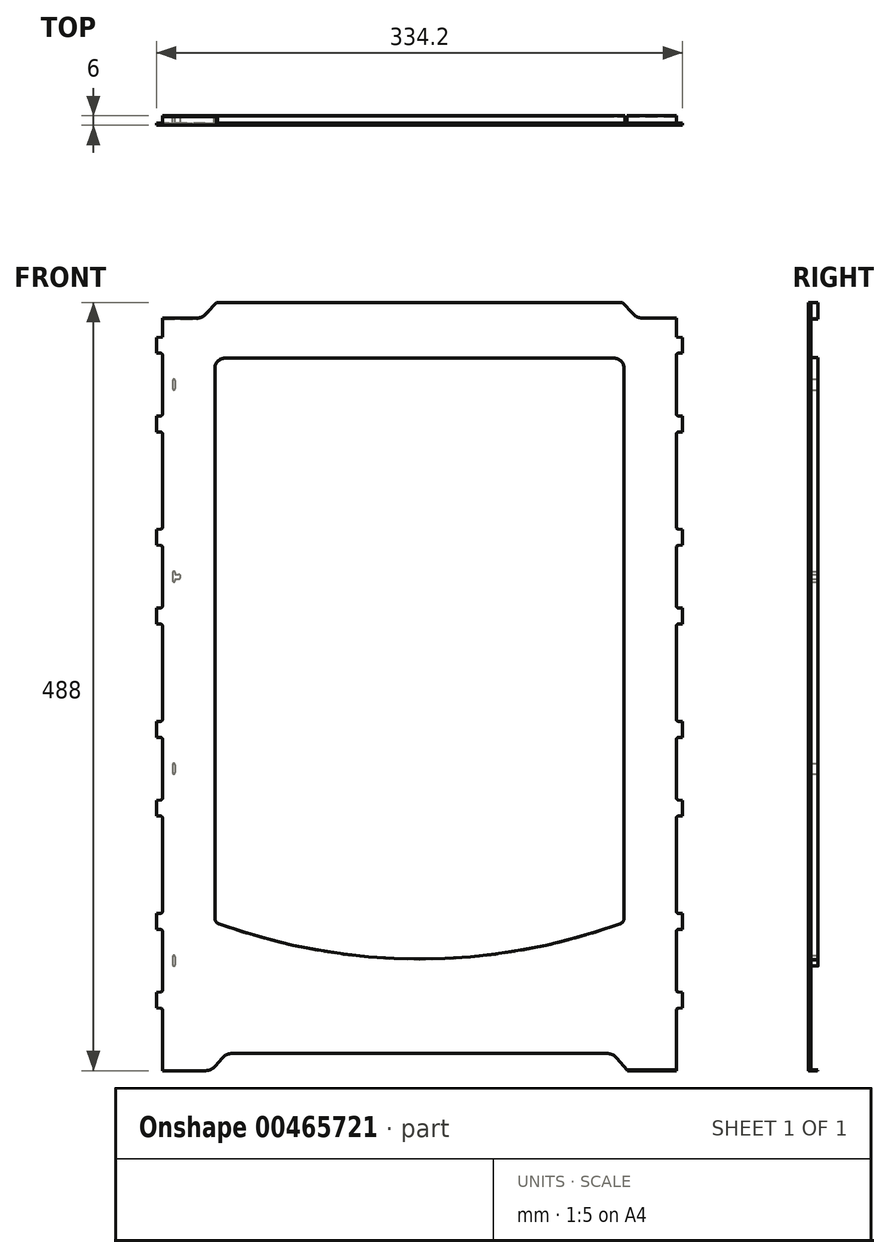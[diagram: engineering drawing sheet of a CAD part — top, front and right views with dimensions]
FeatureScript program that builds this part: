
annotation { "Feature Type Name" : "Feature", "Feature Type Description" : "" }
export const myFeature = defineFeature(function(context is Context, id is Id, definition is map)
    precondition{}
    {
        {
            var Q0;
            Q0=qCreatedBy(makeId("Front.planeOp"),FACE);
            var sketch = newSketch(context, id + "F0", { "sketchPlane" : qUnion([Q0])});
            skLineSegment(sketch, "E0.bottom", {"start": v(163.1, 244) * mm, "end": v(-163.1, 244) * mm});
            skLineSegment(sketch, "E0.top", {"start": v(163.1, -244) * mm, "end": v(-163.1, -244) * mm});
            skLineSegment(sketch, "E0.left", {"start": v(163.1, 244) * mm, "end": v(163.1, -244) * mm});
            skLineSegment(sketch, "E0.right", {"start": v(-163.1, 244) * mm, "end": v(-163.1, -244) * mm});
            skPoint(sketch, "E0.middle", {"position": v(0, 0) * mm});
            skSolve(sketch);
        }
        {
            var Q0;
            Q0=makeQuery(id+"F0.imprint","IMPRINT",FACE,{"disambiguationData":[TD([[makeQuery(id+"F0.imprint","IMPRINT",EDGE,{"derivedFrom":sQuery(id+"F0.wireOp",EDGE,"E0.bottom")}),1.0]])]});
            extrude(context, id + "F1", {"entities" : qUnion([Q0]), "depth" : 6 * mm});
        }
        {
            var Q0;
            Q0=makeQuery(id+"F1.opExtrude","CAP_FACE",FACE,{"disambiguationData":[OSD([sQuery(id+"F0.wireOp",EDGE,"E0.bottom"),sQuery(id+"F0.wireOp",EDGE,"E0.top"),sQuery(id+"F0.wireOp",EDGE,"E0.left"),sQuery(id+"F0.wireOp",EDGE,"E0.right")])],"isStart":false});
            var sketch = newSketch(context, id + "F2", { "sketchPlane" : qUnion([Q0])});
            skLineSegment(sketch, "E1", {"start": v(-167.1, -204.2) * mm, "end": v(-163.1, -204.34) * mm});
            skLineSegment(sketch, "E2", {"start": v(-167.1, -204.2) * mm, "end": v(-167.1, -194.2) * mm});
            skLineSegment(sketch, "E3", {"start": v(-167.1, -199.2) * mm, "end": v(-163.1, -199.2) * mm, "construction": true});
            skLineSegment(sketch, "E4.MirrorCS", {"start": v(-167.1, -194.2) * mm, "end": v(-163.1, -194.06) * mm});
            skLineSegment(sketch, "E5", {"start": v(0, 244) * mm, "end": v(0, -244) * mm, "construction": true});
            skLineSegment(sketch, "E6.MirrorCS", {"start": v(167.1, -204.2) * mm, "end": v(167.1, -194.2) * mm});
            skLineSegment(sketch, "E7.MirrorCS", {"start": v(167.1, -199.2) * mm, "end": v(163.1, -199.2) * mm, "construction": true});
            skLineSegment(sketch, "E8.MirrorCS", {"start": v(167.1, -204.2) * mm, "end": v(163.1, -204.34) * mm});
            skLineSegment(sketch, "E9.MirrorCS", {"start": v(167.1, -194.2) * mm, "end": v(163.1, -194.06) * mm});
            skLineSegment(sketch, "E10", {"start": v(-163.1, -154.34) * mm, "end": v(-167.1, -154.2) * mm});
            skLineSegment(sketch, "E11", {"start": v(-167.1, -154.2) * mm, "end": v(-167.1, -144.2) * mm});
            skLineSegment(sketch, "E12", {"start": v(-167.1, -144.2) * mm, "end": v(-163.1, -144.06) * mm});
            skLineSegment(sketch, "E13", {"start": v(-163.1, -82.34) * mm, "end": v(-167.1, -82.2) * mm});
            skLineSegment(sketch, "E14", {"start": v(-167.1, -82.2) * mm, "end": v(-167.1, -72.2) * mm});
            skLineSegment(sketch, "E15", {"start": v(-167.1, -72.2) * mm, "end": v(-163.1, -72.06) * mm});
            skLineSegment(sketch, "E16", {"start": v(-163.1, -32.34) * mm, "end": v(-167.1, -32.2) * mm});
            skLineSegment(sketch, "E17", {"start": v(-167.1, -32.2) * mm, "end": v(-167.1, -22.2) * mm});
            skLineSegment(sketch, "E18", {"start": v(-167.1, -22.2) * mm, "end": v(-163.1, -22.06) * mm});
            skLineSegment(sketch, "E19", {"start": v(-163.1, 39.66) * mm, "end": v(-167.1, 39.8) * mm});
            skLineSegment(sketch, "E20", {"start": v(-167.1, 39.8) * mm, "end": v(-167.1, 49.8) * mm});
            skLineSegment(sketch, "E21", {"start": v(-167.1, 49.8) * mm, "end": v(-163.1, 49.94) * mm});
            skLineSegment(sketch, "E22", {"start": v(-163.1, 89.66) * mm, "end": v(-167.1, 89.8) * mm});
            skLineSegment(sketch, "E23", {"start": v(-167.1, 89.8) * mm, "end": v(-167.1, 99.8) * mm});
            skLineSegment(sketch, "E24", {"start": v(-167.1, 99.8) * mm, "end": v(-163.1, 99.94) * mm});
            skLineSegment(sketch, "E25", {"start": v(-163.1, 161.66) * mm, "end": v(-167.1, 161.8) * mm});
            skLineSegment(sketch, "E26", {"start": v(-167.1, 161.8) * mm, "end": v(-167.1, 171.8) * mm});
            skLineSegment(sketch, "E27", {"start": v(-167.1, 171.8) * mm, "end": v(-163.1, 171.94) * mm});
            skLineSegment(sketch, "E28", {"start": v(-163.1, 211.66) * mm, "end": v(-167.1, 211.8) * mm});
            skLineSegment(sketch, "E29", {"start": v(-167.1, 211.8) * mm, "end": v(-167.1, 221.8) * mm});
            skLineSegment(sketch, "E30", {"start": v(-167.1, 221.8) * mm, "end": v(-163.1, 221.94) * mm});
            skLineSegment(sketch, "E31.MirrorCS", {"start": v(163.1, 211.66) * mm, "end": v(167.1, 211.8) * mm});
            skLineSegment(sketch, "E32.MirrorCS", {"start": v(167.1, 99.8) * mm, "end": v(163.1, 99.94) * mm});
            skLineSegment(sketch, "E33.MirrorCS", {"start": v(167.1, 221.8) * mm, "end": v(163.1, 221.94) * mm});
            skLineSegment(sketch, "E34.MirrorCS", {"start": v(163.1, -32.34) * mm, "end": v(167.1, -32.2) * mm});
            skLineSegment(sketch, "E35.MirrorCS", {"start": v(163.1, -154.34) * mm, "end": v(167.1, -154.2) * mm});
            skLineSegment(sketch, "E36.MirrorCS", {"start": v(167.1, -154.2) * mm, "end": v(167.1, -144.2) * mm});
            skLineSegment(sketch, "E37.MirrorCS", {"start": v(167.1, -72.2) * mm, "end": v(163.1, -72.06) * mm});
            skLineSegment(sketch, "E38.MirrorCS", {"start": v(167.1, -144.2) * mm, "end": v(163.1, -144.06) * mm});
            skLineSegment(sketch, "E39.MirrorCS", {"start": v(167.1, -82.2) * mm, "end": v(167.1, -72.2) * mm});
            skLineSegment(sketch, "E40.MirrorCS", {"start": v(167.1, 39.8) * mm, "end": v(167.1, 49.8) * mm});
            skLineSegment(sketch, "E41.MirrorCS", {"start": v(167.1, 171.8) * mm, "end": v(163.1, 171.94) * mm});
            skLineSegment(sketch, "E42.MirrorCS", {"start": v(167.1, 161.8) * mm, "end": v(167.1, 171.8) * mm});
            skLineSegment(sketch, "E43.MirrorCS", {"start": v(163.1, -82.34) * mm, "end": v(167.1, -82.2) * mm});
            skLineSegment(sketch, "E44.MirrorCS", {"start": v(167.1, 49.8) * mm, "end": v(163.1, 49.94) * mm});
            skLineSegment(sketch, "E45.MirrorCS", {"start": v(167.1, -22.2) * mm, "end": v(163.1, -22.06) * mm});
            skLineSegment(sketch, "E46.MirrorCS", {"start": v(163.1, 89.66) * mm, "end": v(167.1, 89.8) * mm});
            skLineSegment(sketch, "E47.MirrorCS", {"start": v(163.1, 161.66) * mm, "end": v(167.1, 161.8) * mm});
            skLineSegment(sketch, "E48.MirrorCS", {"start": v(167.1, 211.8) * mm, "end": v(167.1, 221.8) * mm});
            skLineSegment(sketch, "E49.MirrorCS", {"start": v(167.1, 89.8) * mm, "end": v(167.1, 99.8) * mm});
            skLineSegment(sketch, "E50.MirrorCS", {"start": v(167.1, -32.2) * mm, "end": v(167.1, -22.2) * mm});
            skLineSegment(sketch, "E51.MirrorCS", {"start": v(163.1, 39.66) * mm, "end": v(167.1, 39.8) * mm});
            skSolve(sketch);
        }
        {
            var Q0;
            {var subQ0=sQuery(id+"F2.wireOp",EDGE,"E28");Q0=makeQuery(id+"F2.imprint","IMPRINT",FACE,{"disambiguationData":[TD([[makeQuery(id+"F2.imprint","IMPRINT",EDGE,{"derivedFrom":subQ0}),-1.0]])]});}
            var Q1;
            {var subQ0=sQuery(id+"F2.wireOp",EDGE,"E25");Q1=makeQuery(id+"F2.imprint","IMPRINT",FACE,{"disambiguationData":[TD([[makeQuery(id+"F2.imprint","IMPRINT",EDGE,{"derivedFrom":subQ0}),-1.0]])]});}
            var Q2;
            {var subQ0=sQuery(id+"F2.wireOp",EDGE,"E22");Q2=makeQuery(id+"F2.imprint","IMPRINT",FACE,{"disambiguationData":[TD([[makeQuery(id+"F2.imprint","IMPRINT",EDGE,{"derivedFrom":subQ0}),-1.0]])]});}
            var Q3;
            {var subQ0=sQuery(id+"F2.wireOp",EDGE,"E19");Q3=makeQuery(id+"F2.imprint","IMPRINT",FACE,{"disambiguationData":[TD([[makeQuery(id+"F2.imprint","IMPRINT",EDGE,{"derivedFrom":subQ0}),-1.0]])]});}
            var Q4;
            {var subQ0=sQuery(id+"F2.wireOp",EDGE,"E16");Q4=makeQuery(id+"F2.imprint","IMPRINT",FACE,{"disambiguationData":[TD([[makeQuery(id+"F2.imprint","IMPRINT",EDGE,{"derivedFrom":subQ0}),-1.0]])]});}
            var Q5;
            {var subQ0=sQuery(id+"F2.wireOp",EDGE,"E13");Q5=makeQuery(id+"F2.imprint","IMPRINT",FACE,{"disambiguationData":[TD([[makeQuery(id+"F2.imprint","IMPRINT",EDGE,{"derivedFrom":subQ0}),-1.0]])]});}
            var Q6;
            {var subQ0=sQuery(id+"F2.wireOp",EDGE,"E10");Q6=makeQuery(id+"F2.imprint","IMPRINT",FACE,{"disambiguationData":[TD([[makeQuery(id+"F2.imprint","IMPRINT",EDGE,{"derivedFrom":subQ0}),-1.0]])]});}
            var Q7;
            {var subQ0=sQuery(id+"F2.wireOp",EDGE,"E1");Q7=makeQuery(id+"F2.imprint","IMPRINT",FACE,{"disambiguationData":[TD([[makeQuery(id+"F2.imprint","IMPRINT",EDGE,{"derivedFrom":subQ0}),1.0]])]});}
            var Q8;
            Q8=makeQuery(id+"F2.imprint","IMPRINT",FACE,{"disambiguationData":[TD([[makeQuery(id+"F2.imprint","IMPRINT",EDGE,{"derivedFrom":sQuery(id+"F2.wireOp",EDGE,"E6.MirrorCS")}),1.0]])]});
            var Q9;
            {var subQ0=sQuery(id+"F2.wireOp",EDGE,"E35.MirrorCS");Q9=makeQuery(id+"F2.imprint","IMPRINT",FACE,{"disambiguationData":[TD([[makeQuery(id+"F2.imprint","IMPRINT",EDGE,{"derivedFrom":subQ0}),1.0]])]});}
            var Q10;
            {var subQ0=sQuery(id+"F2.wireOp",EDGE,"E37.MirrorCS");Q10=makeQuery(id+"F2.imprint","IMPRINT",FACE,{"disambiguationData":[TD([[makeQuery(id+"F2.imprint","IMPRINT",EDGE,{"derivedFrom":subQ0}),1.0]])]});}
            var Q11;
            {var subQ0=sQuery(id+"F2.wireOp",EDGE,"E34.MirrorCS");Q11=makeQuery(id+"F2.imprint","IMPRINT",FACE,{"disambiguationData":[TD([[makeQuery(id+"F2.imprint","IMPRINT",EDGE,{"derivedFrom":subQ0}),1.0]])]});}
            var Q12;
            Q12=makeQuery(id+"F2.imprint","IMPRINT",FACE,{"disambiguationData":[TD([[makeQuery(id+"F2.imprint","IMPRINT",EDGE,{"derivedFrom":sQuery(id+"F2.wireOp",EDGE,"E40.MirrorCS")}),1.0]])]});
            var Q13;
            {var subQ0=sQuery(id+"F2.wireOp",EDGE,"E32.MirrorCS");Q13=makeQuery(id+"F2.imprint","IMPRINT",FACE,{"disambiguationData":[TD([[makeQuery(id+"F2.imprint","IMPRINT",EDGE,{"derivedFrom":subQ0}),1.0]])]});}
            var Q14;
            {var subQ0=sQuery(id+"F2.wireOp",EDGE,"E41.MirrorCS");Q14=makeQuery(id+"F2.imprint","IMPRINT",FACE,{"disambiguationData":[TD([[makeQuery(id+"F2.imprint","IMPRINT",EDGE,{"derivedFrom":subQ0}),1.0]])]});}
            var Q15;
            {var subQ0=sQuery(id+"F2.wireOp",EDGE,"E31.MirrorCS");Q15=makeQuery(id+"F2.imprint","IMPRINT",FACE,{"disambiguationData":[TD([[makeQuery(id+"F2.imprint","IMPRINT",EDGE,{"derivedFrom":subQ0}),1.0]])]});}
            extrude(context, id + "F3", {"entities" : qUnion([Q0, Q1, Q2, Q3, Q4, Q5, Q6, Q7, Q8, Q9, Q10, Q11, Q12, Q13, Q14, Q15]), "operationType" : NewBodyOperationType.ADD, "oppositeDirection" : true, "depth" : 6 * mm});
        }
        {
            var Q0;
            Q0=makeQuery(id+"F3.opExtrude","SWEPT_EDGE",EDGE,{"disambiguationData":[OSD([sQuery(id+"F0.wireOp",EDGE,"E0.right"),sQuery(id+"F2.wireOp",EDGE,"E1")])]});
            var Q1;
            Q1=makeQuery(id+"F3.opExtrude","SWEPT_EDGE",EDGE,{"disambiguationData":[OSD([sQuery(id+"F0.wireOp",EDGE,"E0.right"),sQuery(id+"F2.wireOp",EDGE,"E4.MirrorCS")])]});
            var Q2;
            Q2=makeQuery(id+"F3.opExtrude","SWEPT_EDGE",EDGE,{"disambiguationData":[OSD([sQuery(id+"F0.wireOp",EDGE,"E0.right"),sQuery(id+"F2.wireOp",EDGE,"E10")])]});
            var Q3;
            Q3=makeQuery(id+"F3.opExtrude","SWEPT_EDGE",EDGE,{"disambiguationData":[OSD([sQuery(id+"F0.wireOp",EDGE,"E0.right"),sQuery(id+"F2.wireOp",EDGE,"E15")])]});
            var Q4;
            Q4=makeQuery(id+"F3.opExtrude","SWEPT_EDGE",EDGE,{"disambiguationData":[OSD([sQuery(id+"F0.wireOp",EDGE,"E0.right"),sQuery(id+"F2.wireOp",EDGE,"E13")])]});
            var Q5;
            Q5=makeQuery(id+"F3.opExtrude","SWEPT_EDGE",EDGE,{"disambiguationData":[OSD([sQuery(id+"F0.wireOp",EDGE,"E0.right"),sQuery(id+"F2.wireOp",EDGE,"E12")])]});
            var Q6;
            Q6=makeQuery(id+"F3.opExtrude","SWEPT_EDGE",EDGE,{"disambiguationData":[OSD([sQuery(id+"F0.wireOp",EDGE,"E0.right"),sQuery(id+"F2.wireOp",EDGE,"E18")])]});
            var Q7;
            Q7=makeQuery(id+"F3.opExtrude","SWEPT_EDGE",EDGE,{"disambiguationData":[OSD([sQuery(id+"F0.wireOp",EDGE,"E0.right"),sQuery(id+"F2.wireOp",EDGE,"E16")])]});
            var Q8;
            Q8=makeQuery(id+"F3.opExtrude","SWEPT_EDGE",EDGE,{"disambiguationData":[OSD([sQuery(id+"F0.wireOp",EDGE,"E0.right"),sQuery(id+"F2.wireOp",EDGE,"E19")])]});
            var Q9;
            Q9=makeQuery(id+"F3.opExtrude","SWEPT_EDGE",EDGE,{"disambiguationData":[OSD([sQuery(id+"F0.wireOp",EDGE,"E0.right"),sQuery(id+"F2.wireOp",EDGE,"E22")])]});
            var Q10;
            Q10=makeQuery(id+"F3.opExtrude","SWEPT_EDGE",EDGE,{"disambiguationData":[OSD([sQuery(id+"F0.wireOp",EDGE,"E0.right"),sQuery(id+"F2.wireOp",EDGE,"E25")])]});
            var Q11;
            Q11=makeQuery(id+"F3.opExtrude","SWEPT_EDGE",EDGE,{"disambiguationData":[OSD([sQuery(id+"F0.wireOp",EDGE,"E0.right"),sQuery(id+"F2.wireOp",EDGE,"E30")])]});
            var Q12;
            Q12=makeQuery(id+"F3.opExtrude","SWEPT_EDGE",EDGE,{"disambiguationData":[OSD([sQuery(id+"F0.wireOp",EDGE,"E0.right"),sQuery(id+"F2.wireOp",EDGE,"E27")])]});
            var Q13;
            Q13=makeQuery(id+"F3.opExtrude","SWEPT_EDGE",EDGE,{"disambiguationData":[OSD([sQuery(id+"F0.wireOp",EDGE,"E0.right"),sQuery(id+"F2.wireOp",EDGE,"E24")])]});
            var Q14;
            Q14=makeQuery(id+"F3.opExtrude","SWEPT_EDGE",EDGE,{"disambiguationData":[OSD([sQuery(id+"F0.wireOp",EDGE,"E0.right"),sQuery(id+"F2.wireOp",EDGE,"E21")])]});
            var Q15;
            Q15=makeQuery(id+"F3.opExtrude","SWEPT_EDGE",EDGE,{"disambiguationData":[OSD([sQuery(id+"F0.wireOp",EDGE,"E0.right"),sQuery(id+"F2.wireOp",EDGE,"E28")])]});
            var Q16;
            Q16=makeQuery(id+"F3.opExtrude","SWEPT_EDGE",EDGE,{"disambiguationData":[OSD([sQuery(id+"F0.wireOp",EDGE,"E0.left"),sQuery(id+"F2.wireOp",EDGE,"E33.MirrorCS")])]});
            var Q17;
            Q17=makeQuery(id+"F3.opExtrude","SWEPT_EDGE",EDGE,{"disambiguationData":[OSD([sQuery(id+"F0.wireOp",EDGE,"E0.left"),sQuery(id+"F2.wireOp",EDGE,"E41.MirrorCS")])]});
            var Q18;
            Q18=makeQuery(id+"F3.opExtrude","SWEPT_EDGE",EDGE,{"disambiguationData":[OSD([sQuery(id+"F0.wireOp",EDGE,"E0.left"),sQuery(id+"F2.wireOp",EDGE,"E32.MirrorCS")])]});
            var Q19;
            Q19=makeQuery(id+"F3.opExtrude","SWEPT_EDGE",EDGE,{"disambiguationData":[OSD([sQuery(id+"F0.wireOp",EDGE,"E0.left"),sQuery(id+"F2.wireOp",EDGE,"E44.MirrorCS")])]});
            var Q20;
            Q20=makeQuery(id+"F3.opExtrude","SWEPT_EDGE",EDGE,{"disambiguationData":[OSD([sQuery(id+"F0.wireOp",EDGE,"E0.left"),sQuery(id+"F2.wireOp",EDGE,"E45.MirrorCS")])]});
            var Q21;
            Q21=makeQuery(id+"F3.opExtrude","SWEPT_EDGE",EDGE,{"disambiguationData":[OSD([sQuery(id+"F0.wireOp",EDGE,"E0.left"),sQuery(id+"F2.wireOp",EDGE,"E37.MirrorCS")])]});
            var Q22;
            Q22=makeQuery(id+"F3.opExtrude","SWEPT_EDGE",EDGE,{"disambiguationData":[OSD([sQuery(id+"F0.wireOp",EDGE,"E0.left"),sQuery(id+"F2.wireOp",EDGE,"E9.MirrorCS")])]});
            var Q23;
            Q23=makeQuery(id+"F3.opExtrude","SWEPT_EDGE",EDGE,{"disambiguationData":[OSD([sQuery(id+"F0.wireOp",EDGE,"E0.left"),sQuery(id+"F2.wireOp",EDGE,"E38.MirrorCS")])]});
            var Q24;
            Q24=makeQuery(id+"F3.opExtrude","SWEPT_EDGE",EDGE,{"disambiguationData":[OSD([sQuery(id+"F0.wireOp",EDGE,"E0.left"),sQuery(id+"F2.wireOp",EDGE,"E8.MirrorCS")])]});
            var Q25;
            Q25=makeQuery(id+"F3.opExtrude","SWEPT_EDGE",EDGE,{"disambiguationData":[OSD([sQuery(id+"F0.wireOp",EDGE,"E0.left"),sQuery(id+"F2.wireOp",EDGE,"E35.MirrorCS")])]});
            var Q26;
            Q26=makeQuery(id+"F3.opExtrude","SWEPT_EDGE",EDGE,{"disambiguationData":[OSD([sQuery(id+"F0.wireOp",EDGE,"E0.left"),sQuery(id+"F2.wireOp",EDGE,"E43.MirrorCS")])]});
            var Q27;
            Q27=makeQuery(id+"F3.opExtrude","SWEPT_EDGE",EDGE,{"disambiguationData":[OSD([sQuery(id+"F0.wireOp",EDGE,"E0.left"),sQuery(id+"F2.wireOp",EDGE,"E34.MirrorCS")])]});
            var Q28;
            Q28=makeQuery(id+"F3.opExtrude","SWEPT_EDGE",EDGE,{"disambiguationData":[OSD([sQuery(id+"F0.wireOp",EDGE,"E0.left"),sQuery(id+"F2.wireOp",EDGE,"E51.MirrorCS")])]});
            var Q29;
            Q29=makeQuery(id+"F3.opExtrude","SWEPT_EDGE",EDGE,{"disambiguationData":[OSD([sQuery(id+"F0.wireOp",EDGE,"E0.left"),sQuery(id+"F2.wireOp",EDGE,"E46.MirrorCS")])]});
            var Q30;
            Q30=makeQuery(id+"F3.opExtrude","SWEPT_EDGE",EDGE,{"disambiguationData":[OSD([sQuery(id+"F0.wireOp",EDGE,"E0.left"),sQuery(id+"F2.wireOp",EDGE,"E47.MirrorCS")])]});
            var Q31;
            Q31=makeQuery(id+"F3.opExtrude","SWEPT_EDGE",EDGE,{"disambiguationData":[OSD([sQuery(id+"F0.wireOp",EDGE,"E0.left"),sQuery(id+"F2.wireOp",EDGE,"E31.MirrorCS")])]});
            fillet(context, id + "F4", {"entities" : qUnion([Q0, Q1, Q2, Q3, Q4, Q5, Q6, Q7, Q8, Q9, Q10, Q11, Q12, Q13, Q14, Q15, Q16, Q17, Q18, Q19, Q20, Q21, Q22, Q23, Q24, Q25, Q26, Q27, Q28, Q29, Q30, Q31]), "radius" : 1.5 * mm, "tangentPropagation" : true, "allowEdgeOverflow" : false});
        }
        {
            var Q0;
            {var subQ0=sQuery(id+"F0.wireOp",EDGE,"E0.left");var subQ1=sQuery(id+"F0.wireOp",EDGE,"E0.right");Q0=makeQuery(id+"F3.boolean.opBoolean","MERGE",FACE,{"derivedFrom":[makeQuery(id+"F1.opExtrude","CAP_FACE",FACE,{"disambiguationData":[OSD([sQuery(id+"F0.wireOp",EDGE,"E0.bottom"),sQuery(id+"F0.wireOp",EDGE,"E0.top"),subQ0,subQ1])],"isStart":false}),makeQuery(id+"F3.opExtrude","CAP_FACE",FACE,{"disambiguationData":[OSD([subQ1,sQuery(id+"F2.wireOp",EDGE,"E1"),sQuery(id+"F2.wireOp",EDGE,"E2"),sQuery(id+"F2.wireOp",EDGE,"E4.MirrorCS")])],"isStart":true}),makeQuery(id+"F3.opExtrude","CAP_FACE",FACE,{"disambiguationData":[OSD([subQ0,sQuery(id+"F2.wireOp",EDGE,"E6.MirrorCS"),sQuery(id+"F2.wireOp",EDGE,"E8.MirrorCS"),sQuery(id+"F2.wireOp",EDGE,"E9.MirrorCS")])],"isStart":true}),makeQuery(id+"F3.opExtrude","CAP_FACE",FACE,{"disambiguationData":[OSD([subQ1,sQuery(id+"F2.wireOp",EDGE,"E10"),sQuery(id+"F2.wireOp",EDGE,"E11"),sQuery(id+"F2.wireOp",EDGE,"E12")])],"isStart":true}),makeQuery(id+"F3.opExtrude","CAP_FACE",FACE,{"disambiguationData":[OSD([subQ1,sQuery(id+"F2.wireOp",EDGE,"E13"),sQuery(id+"F2.wireOp",EDGE,"E14"),sQuery(id+"F2.wireOp",EDGE,"E15")])],"isStart":true}),makeQuery(id+"F3.opExtrude","CAP_FACE",FACE,{"disambiguationData":[OSD([subQ1,sQuery(id+"F2.wireOp",EDGE,"E16"),sQuery(id+"F2.wireOp",EDGE,"E17"),sQuery(id+"F2.wireOp",EDGE,"E18")])],"isStart":true}),makeQuery(id+"F3.opExtrude","CAP_FACE",FACE,{"disambiguationData":[OSD([subQ1,sQuery(id+"F2.wireOp",EDGE,"E19"),sQuery(id+"F2.wireOp",EDGE,"E20"),sQuery(id+"F2.wireOp",EDGE,"E21")])],"isStart":true}),makeQuery(id+"F3.opExtrude","CAP_FACE",FACE,{"disambiguationData":[OSD([subQ1,sQuery(id+"F2.wireOp",EDGE,"E22"),sQuery(id+"F2.wireOp",EDGE,"E23"),sQuery(id+"F2.wireOp",EDGE,"E24")])],"isStart":true}),makeQuery(id+"F3.opExtrude","CAP_FACE",FACE,{"disambiguationData":[OSD([subQ1,sQuery(id+"F2.wireOp",EDGE,"E25"),sQuery(id+"F2.wireOp",EDGE,"E26"),sQuery(id+"F2.wireOp",EDGE,"E27")])],"isStart":true}),makeQuery(id+"F3.opExtrude","CAP_FACE",FACE,{"disambiguationData":[OSD([subQ1,sQuery(id+"F2.wireOp",EDGE,"E28"),sQuery(id+"F2.wireOp",EDGE,"E29"),sQuery(id+"F2.wireOp",EDGE,"E30")])],"isStart":true}),makeQuery(id+"F3.opExtrude","CAP_FACE",FACE,{"disambiguationData":[OSD([subQ0,sQuery(id+"F2.wireOp",EDGE,"E31.MirrorCS"),sQuery(id+"F2.wireOp",EDGE,"E33.MirrorCS"),sQuery(id+"F2.wireOp",EDGE,"E48.MirrorCS")])],"isStart":true}),makeQuery(id+"F3.opExtrude","CAP_FACE",FACE,{"disambiguationData":[OSD([subQ0,sQuery(id+"F2.wireOp",EDGE,"E32.MirrorCS"),sQuery(id+"F2.wireOp",EDGE,"E46.MirrorCS"),sQuery(id+"F2.wireOp",EDGE,"E49.MirrorCS")])],"isStart":true}),makeQuery(id+"F3.opExtrude","CAP_FACE",FACE,{"disambiguationData":[OSD([subQ0,sQuery(id+"F2.wireOp",EDGE,"E34.MirrorCS"),sQuery(id+"F2.wireOp",EDGE,"E45.MirrorCS"),sQuery(id+"F2.wireOp",EDGE,"E50.MirrorCS")])],"isStart":true}),makeQuery(id+"F3.opExtrude","CAP_FACE",FACE,{"disambiguationData":[OSD([subQ0,sQuery(id+"F2.wireOp",EDGE,"E35.MirrorCS"),sQuery(id+"F2.wireOp",EDGE,"E36.MirrorCS"),sQuery(id+"F2.wireOp",EDGE,"E38.MirrorCS")])],"isStart":true}),makeQuery(id+"F3.opExtrude","CAP_FACE",FACE,{"disambiguationData":[OSD([subQ0,sQuery(id+"F2.wireOp",EDGE,"E37.MirrorCS"),sQuery(id+"F2.wireOp",EDGE,"E39.MirrorCS"),sQuery(id+"F2.wireOp",EDGE,"E43.MirrorCS")])],"isStart":true}),makeQuery(id+"F3.opExtrude","CAP_FACE",FACE,{"disambiguationData":[OSD([subQ0,sQuery(id+"F2.wireOp",EDGE,"E40.MirrorCS"),sQuery(id+"F2.wireOp",EDGE,"E44.MirrorCS"),sQuery(id+"F2.wireOp",EDGE,"E51.MirrorCS")])],"isStart":true}),makeQuery(id+"F3.opExtrude","CAP_FACE",FACE,{"disambiguationData":[OSD([subQ0,sQuery(id+"F2.wireOp",EDGE,"E41.MirrorCS"),sQuery(id+"F2.wireOp",EDGE,"E42.MirrorCS"),sQuery(id+"F2.wireOp",EDGE,"E47.MirrorCS")])],"isStart":true})]});}
            var sketch = newSketch(context, id + "F5", { "sketchPlane" : qUnion([Q0])});
            skLineSegment(sketch, "E52.bottom", {"start": v(130, -173) * mm, "end": v(-130, -173) * mm, "construction": true});
            skLineSegment(sketch, "E52.top", {"start": v(130, 208.5) * mm, "end": v(-130, 208.5) * mm});
            skLineSegment(sketch, "E52.left", {"start": v(130, -173) * mm, "end": v(130, 208.5) * mm});
            skLineSegment(sketch, "E52.right", {"start": v(-130, -173) * mm, "end": v(-130, 208.5) * mm});
            skPoint(sketch, "E52.middle", {"position": v(0, 17.75) * mm});
            skArc(sketch, "E53", {"start": v(-130, -149.75) * mm, "mid": v(0, -173) * mm, "end": v(130, -149.75) * mm});
            skSolve(sketch);
        }
        {
            var Q0;
            {var subQ0=sQuery(id+"F5.wireOp",EDGE,"E52.top");Q0=makeQuery(id+"F5.imprint","IMPRINT",FACE,{"disambiguationData":[TD([[makeQuery(id+"F5.imprint","IMPRINT",EDGE,{"derivedFrom":subQ0}),1.0]])]});}
            extrude(context, id + "F6", {"entities" : qUnion([Q0]), "operationType" : NewBodyOperationType.REMOVE, "oppositeDirection" : true, "depth" : 25 * mm});
        }
        {
            var Q0;
            Q0=makeQuery(id+"F6.boolean.opBoolean","COPY",EDGE,{"derivedFrom":makeQuery(id+"F6.opExtrude","SWEPT_EDGE",EDGE,{"disambiguationData":[OSD([sQuery(id+"F5.wireOp",EDGE,"E52.top"),sQuery(id+"F5.wireOp",EDGE,"E52.right")])]})});
            var Q1;
            Q1=makeQuery(id+"F6.boolean.opBoolean","COPY",EDGE,{"derivedFrom":makeQuery(id+"F6.opExtrude","SWEPT_EDGE",EDGE,{"disambiguationData":[OSD([sQuery(id+"F5.wireOp",EDGE,"E52.top"),sQuery(id+"F5.wireOp",EDGE,"E52.left")])]})});
            fillet(context, id + "F7", {"entities" : qUnion([Q0, Q1]), "radius" : 6.5 * mm, "tangentPropagation" : true, "allowEdgeOverflow" : false});
        }
        {
            var Q0;
            Q0=makeQuery(id+"F6.boolean.opBoolean","COPY",EDGE,{"derivedFrom":makeQuery(id+"F6.opExtrude","SWEPT_EDGE",EDGE,{"disambiguationData":[OSD([sQuery(id+"F5.wireOp",EDGE,"E52.left"),sQuery(id+"F5.wireOp",EDGE,"E53")])]})});
            var Q1;
            Q1=makeQuery(id+"F6.boolean.opBoolean","COPY",EDGE,{"derivedFrom":makeQuery(id+"F6.opExtrude","SWEPT_EDGE",EDGE,{"disambiguationData":[OSD([sQuery(id+"F5.wireOp",EDGE,"E52.right"),sQuery(id+"F5.wireOp",EDGE,"E53")])]})});
            fillet(context, id + "F8", {"entities" : qUnion([Q0, Q1]), "radius" : 4 * mm, "tangentPropagation" : true, "allowEdgeOverflow" : false});
        }
        {
            var Q0;
            {var subQ0=sQuery(id+"F0.wireOp",EDGE,"E0.left");var subQ1=sQuery(id+"F0.wireOp",EDGE,"E0.right");Q0=makeQuery(id+"F6.boolean.opBoolean","INTERSECT",EDGE,{"derivedFrom":[makeQuery(id+"F3.boolean.opBoolean","MERGE",FACE,{"derivedFrom":[makeQuery(id+"F1.opExtrude","CAP_FACE",FACE,{"disambiguationData":[OSD([sQuery(id+"F0.wireOp",EDGE,"E0.bottom"),sQuery(id+"F0.wireOp",EDGE,"E0.top"),subQ0,subQ1])],"isStart":true}),makeQuery(id+"F3.opExtrude","CAP_FACE",FACE,{"disambiguationData":[OSD([subQ1,sQuery(id+"F2.wireOp",EDGE,"E1"),sQuery(id+"F2.wireOp",EDGE,"E2"),sQuery(id+"F2.wireOp",EDGE,"E4.MirrorCS")])],"isStart":false}),makeQuery(id+"F3.opExtrude","CAP_FACE",FACE,{"disambiguationData":[OSD([subQ0,sQuery(id+"F2.wireOp",EDGE,"E6.MirrorCS"),sQuery(id+"F2.wireOp",EDGE,"E8.MirrorCS"),sQuery(id+"F2.wireOp",EDGE,"E9.MirrorCS")])],"isStart":false}),makeQuery(id+"F3.opExtrude","CAP_FACE",FACE,{"disambiguationData":[OSD([subQ1,sQuery(id+"F2.wireOp",EDGE,"E10"),sQuery(id+"F2.wireOp",EDGE,"E11"),sQuery(id+"F2.wireOp",EDGE,"E12")])],"isStart":false}),makeQuery(id+"F3.opExtrude","CAP_FACE",FACE,{"disambiguationData":[OSD([subQ1,sQuery(id+"F2.wireOp",EDGE,"E13"),sQuery(id+"F2.wireOp",EDGE,"E14"),sQuery(id+"F2.wireOp",EDGE,"E15")])],"isStart":false}),makeQuery(id+"F3.opExtrude","CAP_FACE",FACE,{"disambiguationData":[OSD([subQ1,sQuery(id+"F2.wireOp",EDGE,"E16"),sQuery(id+"F2.wireOp",EDGE,"E17"),sQuery(id+"F2.wireOp",EDGE,"E18")])],"isStart":false}),makeQuery(id+"F3.opExtrude","CAP_FACE",FACE,{"disambiguationData":[OSD([subQ1,sQuery(id+"F2.wireOp",EDGE,"E19"),sQuery(id+"F2.wireOp",EDGE,"E20"),sQuery(id+"F2.wireOp",EDGE,"E21")])],"isStart":false}),makeQuery(id+"F3.opExtrude","CAP_FACE",FACE,{"disambiguationData":[OSD([subQ1,sQuery(id+"F2.wireOp",EDGE,"E22"),sQuery(id+"F2.wireOp",EDGE,"E23"),sQuery(id+"F2.wireOp",EDGE,"E24")])],"isStart":false}),makeQuery(id+"F3.opExtrude","CAP_FACE",FACE,{"disambiguationData":[OSD([subQ1,sQuery(id+"F2.wireOp",EDGE,"E25"),sQuery(id+"F2.wireOp",EDGE,"E26"),sQuery(id+"F2.wireOp",EDGE,"E27")])],"isStart":false}),makeQuery(id+"F3.opExtrude","CAP_FACE",FACE,{"disambiguationData":[OSD([subQ1,sQuery(id+"F2.wireOp",EDGE,"E28"),sQuery(id+"F2.wireOp",EDGE,"E29"),sQuery(id+"F2.wireOp",EDGE,"E30")])],"isStart":false}),makeQuery(id+"F3.opExtrude","CAP_FACE",FACE,{"disambiguationData":[OSD([subQ0,sQuery(id+"F2.wireOp",EDGE,"E31.MirrorCS"),sQuery(id+"F2.wireOp",EDGE,"E33.MirrorCS"),sQuery(id+"F2.wireOp",EDGE,"E48.MirrorCS")])],"isStart":false}),makeQuery(id+"F3.opExtrude","CAP_FACE",FACE,{"disambiguationData":[OSD([subQ0,sQuery(id+"F2.wireOp",EDGE,"E32.MirrorCS"),sQuery(id+"F2.wireOp",EDGE,"E46.MirrorCS"),sQuery(id+"F2.wireOp",EDGE,"E49.MirrorCS")])],"isStart":false}),makeQuery(id+"F3.opExtrude","CAP_FACE",FACE,{"disambiguationData":[OSD([subQ0,sQuery(id+"F2.wireOp",EDGE,"E34.MirrorCS"),sQuery(id+"F2.wireOp",EDGE,"E45.MirrorCS"),sQuery(id+"F2.wireOp",EDGE,"E50.MirrorCS")])],"isStart":false}),makeQuery(id+"F3.opExtrude","CAP_FACE",FACE,{"disambiguationData":[OSD([subQ0,sQuery(id+"F2.wireOp",EDGE,"E35.MirrorCS"),sQuery(id+"F2.wireOp",EDGE,"E36.MirrorCS"),sQuery(id+"F2.wireOp",EDGE,"E38.MirrorCS")])],"isStart":false}),makeQuery(id+"F3.opExtrude","CAP_FACE",FACE,{"disambiguationData":[OSD([subQ0,sQuery(id+"F2.wireOp",EDGE,"E37.MirrorCS"),sQuery(id+"F2.wireOp",EDGE,"E39.MirrorCS"),sQuery(id+"F2.wireOp",EDGE,"E43.MirrorCS")])],"isStart":false}),makeQuery(id+"F3.opExtrude","CAP_FACE",FACE,{"disambiguationData":[OSD([subQ0,sQuery(id+"F2.wireOp",EDGE,"E40.MirrorCS"),sQuery(id+"F2.wireOp",EDGE,"E44.MirrorCS"),sQuery(id+"F2.wireOp",EDGE,"E51.MirrorCS")])],"isStart":false}),makeQuery(id+"F3.opExtrude","CAP_FACE",FACE,{"disambiguationData":[OSD([subQ0,sQuery(id+"F2.wireOp",EDGE,"E41.MirrorCS"),sQuery(id+"F2.wireOp",EDGE,"E42.MirrorCS"),sQuery(id+"F2.wireOp",EDGE,"E47.MirrorCS")])],"isStart":false})]}),makeQuery(id+"F6.opExtrude","SWEPT_FACE",FACE,{"disambiguationData":[OSD([sQuery(id+"F5.wireOp",EDGE,"E52.left")])]})]});}
            var Q1;
            Q1=makeQuery(id+"F6.boolean.opBoolean","COPY",EDGE,{"derivedFrom":makeQuery(id+"F6.opExtrude","CAP_EDGE",EDGE,{"disambiguationData":[OSD([sQuery(id+"F5.wireOp",EDGE,"E52.left")])],"isStart":true})});
            chamfer(context, id + "F9", {"entities" : qUnion([Q0, Q1]), "width" : .5 * mm, "tangentPropagation" : true});
        }
        {
            var Q0;
            {var subQ0=sQuery(id+"F0.wireOp",EDGE,"E0.left");var subQ1=sQuery(id+"F0.wireOp",EDGE,"E0.right");Q0=makeQuery(id+"F3.boolean.opBoolean","MERGE",FACE,{"derivedFrom":[makeQuery(id+"F1.opExtrude","CAP_FACE",FACE,{"disambiguationData":[OSD([sQuery(id+"F0.wireOp",EDGE,"E0.bottom"),sQuery(id+"F0.wireOp",EDGE,"E0.top"),subQ0,subQ1])],"isStart":false}),makeQuery(id+"F3.opExtrude","CAP_FACE",FACE,{"disambiguationData":[OSD([subQ1,sQuery(id+"F2.wireOp",EDGE,"E1"),sQuery(id+"F2.wireOp",EDGE,"E2"),sQuery(id+"F2.wireOp",EDGE,"E4.MirrorCS")])],"isStart":true}),makeQuery(id+"F3.opExtrude","CAP_FACE",FACE,{"disambiguationData":[OSD([subQ0,sQuery(id+"F2.wireOp",EDGE,"E6.MirrorCS"),sQuery(id+"F2.wireOp",EDGE,"E8.MirrorCS"),sQuery(id+"F2.wireOp",EDGE,"E9.MirrorCS")])],"isStart":true}),makeQuery(id+"F3.opExtrude","CAP_FACE",FACE,{"disambiguationData":[OSD([subQ1,sQuery(id+"F2.wireOp",EDGE,"E10"),sQuery(id+"F2.wireOp",EDGE,"E11"),sQuery(id+"F2.wireOp",EDGE,"E12")])],"isStart":true}),makeQuery(id+"F3.opExtrude","CAP_FACE",FACE,{"disambiguationData":[OSD([subQ1,sQuery(id+"F2.wireOp",EDGE,"E13"),sQuery(id+"F2.wireOp",EDGE,"E14"),sQuery(id+"F2.wireOp",EDGE,"E15")])],"isStart":true}),makeQuery(id+"F3.opExtrude","CAP_FACE",FACE,{"disambiguationData":[OSD([subQ1,sQuery(id+"F2.wireOp",EDGE,"E16"),sQuery(id+"F2.wireOp",EDGE,"E17"),sQuery(id+"F2.wireOp",EDGE,"E18")])],"isStart":true}),makeQuery(id+"F3.opExtrude","CAP_FACE",FACE,{"disambiguationData":[OSD([subQ1,sQuery(id+"F2.wireOp",EDGE,"E19"),sQuery(id+"F2.wireOp",EDGE,"E20"),sQuery(id+"F2.wireOp",EDGE,"E21")])],"isStart":true}),makeQuery(id+"F3.opExtrude","CAP_FACE",FACE,{"disambiguationData":[OSD([subQ1,sQuery(id+"F2.wireOp",EDGE,"E22"),sQuery(id+"F2.wireOp",EDGE,"E23"),sQuery(id+"F2.wireOp",EDGE,"E24")])],"isStart":true}),makeQuery(id+"F3.opExtrude","CAP_FACE",FACE,{"disambiguationData":[OSD([subQ1,sQuery(id+"F2.wireOp",EDGE,"E25"),sQuery(id+"F2.wireOp",EDGE,"E26"),sQuery(id+"F2.wireOp",EDGE,"E27")])],"isStart":true}),makeQuery(id+"F3.opExtrude","CAP_FACE",FACE,{"disambiguationData":[OSD([subQ1,sQuery(id+"F2.wireOp",EDGE,"E28"),sQuery(id+"F2.wireOp",EDGE,"E29"),sQuery(id+"F2.wireOp",EDGE,"E30")])],"isStart":true}),makeQuery(id+"F3.opExtrude","CAP_FACE",FACE,{"disambiguationData":[OSD([subQ0,sQuery(id+"F2.wireOp",EDGE,"E31.MirrorCS"),sQuery(id+"F2.wireOp",EDGE,"E33.MirrorCS"),sQuery(id+"F2.wireOp",EDGE,"E48.MirrorCS")])],"isStart":true}),makeQuery(id+"F3.opExtrude","CAP_FACE",FACE,{"disambiguationData":[OSD([subQ0,sQuery(id+"F2.wireOp",EDGE,"E32.MirrorCS"),sQuery(id+"F2.wireOp",EDGE,"E46.MirrorCS"),sQuery(id+"F2.wireOp",EDGE,"E49.MirrorCS")])],"isStart":true}),makeQuery(id+"F3.opExtrude","CAP_FACE",FACE,{"disambiguationData":[OSD([subQ0,sQuery(id+"F2.wireOp",EDGE,"E34.MirrorCS"),sQuery(id+"F2.wireOp",EDGE,"E45.MirrorCS"),sQuery(id+"F2.wireOp",EDGE,"E50.MirrorCS")])],"isStart":true}),makeQuery(id+"F3.opExtrude","CAP_FACE",FACE,{"disambiguationData":[OSD([subQ0,sQuery(id+"F2.wireOp",EDGE,"E35.MirrorCS"),sQuery(id+"F2.wireOp",EDGE,"E36.MirrorCS"),sQuery(id+"F2.wireOp",EDGE,"E38.MirrorCS")])],"isStart":true}),makeQuery(id+"F3.opExtrude","CAP_FACE",FACE,{"disambiguationData":[OSD([subQ0,sQuery(id+"F2.wireOp",EDGE,"E37.MirrorCS"),sQuery(id+"F2.wireOp",EDGE,"E39.MirrorCS"),sQuery(id+"F2.wireOp",EDGE,"E43.MirrorCS")])],"isStart":true}),makeQuery(id+"F3.opExtrude","CAP_FACE",FACE,{"disambiguationData":[OSD([subQ0,sQuery(id+"F2.wireOp",EDGE,"E40.MirrorCS"),sQuery(id+"F2.wireOp",EDGE,"E44.MirrorCS"),sQuery(id+"F2.wireOp",EDGE,"E51.MirrorCS")])],"isStart":true}),makeQuery(id+"F3.opExtrude","CAP_FACE",FACE,{"disambiguationData":[OSD([subQ0,sQuery(id+"F2.wireOp",EDGE,"E41.MirrorCS"),sQuery(id+"F2.wireOp",EDGE,"E42.MirrorCS"),sQuery(id+"F2.wireOp",EDGE,"E47.MirrorCS")])],"isStart":true})]});}
            var sketch = newSketch(context, id + "F10", { "sketchPlane" : qUnion([Q0])});
            skLineSegment(sketch, "E54", {"start": v(-132.13, -244) * mm, "end": v(-122.98, -233.1) * mm});
            skLineSegment(sketch, "E55", {"start": v(-122.98, -233.1) * mm, "end": v(122.98, -233.09) * mm});
            skLineSegment(sketch, "E56", {"start": v(122.98, -233.09) * mm, "end": v(132.13, -244) * mm});
            skLineSegment(sketch, "E57", {"start": v(0, -233.1) * mm, "end": v(0, 0) * mm, "construction": true});
            skSolve(sketch);
        }
        {
            var Q0;
            {var subQ0=sQuery(id+"F10.wireOp",EDGE,"E54");Q0=makeQuery(id+"F10.imprint","IMPRINT",FACE,{"disambiguationData":[TD([[makeQuery(id+"F10.imprint","IMPRINT",EDGE,{"derivedFrom":subQ0}),-1.0]])]});}
            extrude(context, id + "F11", {"entities" : qUnion([Q0]), "operationType" : NewBodyOperationType.REMOVE, "oppositeDirection" : true, "depth" : 25 * mm});
        }
        {
            var Q0;
            Q0=makeQuery(id+"F11.boolean.opBoolean","COPY",EDGE,{"derivedFrom":makeQuery(id+"F11.opExtrude","SWEPT_EDGE",EDGE,{"disambiguationData":[OSD([sQuery(id+"F0.wireOp",EDGE,"E0.top"),sQuery(id+"F10.wireOp",EDGE,"E54")])]})});
            var Q1;
            Q1=makeQuery(id+"F11.boolean.opBoolean","COPY",EDGE,{"derivedFrom":makeQuery(id+"F11.opExtrude","SWEPT_EDGE",EDGE,{"disambiguationData":[OSD([sQuery(id+"F10.wireOp",EDGE,"E54"),sQuery(id+"F10.wireOp",EDGE,"E55")])]})});
            var Q2;
            Q2=makeQuery(id+"F11.boolean.opBoolean","COPY",EDGE,{"derivedFrom":makeQuery(id+"F11.opExtrude","SWEPT_EDGE",EDGE,{"disambiguationData":[OSD([sQuery(id+"F10.wireOp",EDGE,"E55"),sQuery(id+"F10.wireOp",EDGE,"E56")])]})});
            var Q3;
            Q3=makeQuery(id+"F11.boolean.opBoolean","COPY",EDGE,{"derivedFrom":makeQuery(id+"F11.opExtrude","SWEPT_EDGE",EDGE,{"disambiguationData":[OSD([sQuery(id+"F0.wireOp",EDGE,"E0.top"),sQuery(id+"F10.wireOp",EDGE,"E56")])]})});
            fillet(context, id + "F12", {"entities" : qUnion([Q0, Q1, Q2, Q3]), "radius" : 8.5 * mm, "tangentPropagation" : true, "allowEdgeOverflow" : false});
        }
        {
            var Q0;
            {var subQ1=sQuery(id+"F0.wireOp",EDGE,"E0.left");var subQ2=sQuery(id+"F0.wireOp",EDGE,"E0.top");Q0=makeQuery(id+"F11.boolean.opBoolean","SPLIT",EDGE,{"disambiguationData":[TD([makeQuery(id+"F1.opExtrude","SWEPT_FACE",FACE,{"disambiguationData":[OSD([subQ1])]})])],"derivedFrom":makeQuery(id+"F1.opExtrude","CAP_EDGE",EDGE,{"disambiguationData":[OSD([subQ2])],"isStart":true})});}
            var Q1;
            {var subQ1=sQuery(id+"F0.wireOp",EDGE,"E0.left");var subQ2=sQuery(id+"F0.wireOp",EDGE,"E0.top");Q1=makeQuery(id+"F11.boolean.opBoolean","SPLIT",EDGE,{"disambiguationData":[TD([makeQuery(id+"F1.opExtrude","SWEPT_FACE",FACE,{"disambiguationData":[OSD([subQ1])]})])],"derivedFrom":makeQuery(id+"F1.opExtrude","CAP_EDGE",EDGE,{"disambiguationData":[OSD([subQ2])],"isStart":false})});}
            chamfer(context, id + "F13", {"entities" : qUnion([Q0, Q1]), "width" : .5 * mm, "tangentPropagation" : true});
        }
        {
            var Q0;
            {var subQ0=sQuery(id+"F0.wireOp",EDGE,"E0.left");var subQ1=sQuery(id+"F0.wireOp",EDGE,"E0.right");Q0=makeQuery(id+"F3.boolean.opBoolean","MERGE",FACE,{"derivedFrom":[makeQuery(id+"F1.opExtrude","CAP_FACE",FACE,{"disambiguationData":[OSD([sQuery(id+"F0.wireOp",EDGE,"E0.bottom"),sQuery(id+"F0.wireOp",EDGE,"E0.top"),subQ0,subQ1])],"isStart":false}),makeQuery(id+"F3.opExtrude","CAP_FACE",FACE,{"disambiguationData":[OSD([subQ1,sQuery(id+"F2.wireOp",EDGE,"E1"),sQuery(id+"F2.wireOp",EDGE,"E2"),sQuery(id+"F2.wireOp",EDGE,"E4.MirrorCS")])],"isStart":true}),makeQuery(id+"F3.opExtrude","CAP_FACE",FACE,{"disambiguationData":[OSD([subQ0,sQuery(id+"F2.wireOp",EDGE,"E6.MirrorCS"),sQuery(id+"F2.wireOp",EDGE,"E8.MirrorCS"),sQuery(id+"F2.wireOp",EDGE,"E9.MirrorCS")])],"isStart":true}),makeQuery(id+"F3.opExtrude","CAP_FACE",FACE,{"disambiguationData":[OSD([subQ1,sQuery(id+"F2.wireOp",EDGE,"E10"),sQuery(id+"F2.wireOp",EDGE,"E11"),sQuery(id+"F2.wireOp",EDGE,"E12")])],"isStart":true}),makeQuery(id+"F3.opExtrude","CAP_FACE",FACE,{"disambiguationData":[OSD([subQ1,sQuery(id+"F2.wireOp",EDGE,"E13"),sQuery(id+"F2.wireOp",EDGE,"E14"),sQuery(id+"F2.wireOp",EDGE,"E15")])],"isStart":true}),makeQuery(id+"F3.opExtrude","CAP_FACE",FACE,{"disambiguationData":[OSD([subQ1,sQuery(id+"F2.wireOp",EDGE,"E16"),sQuery(id+"F2.wireOp",EDGE,"E17"),sQuery(id+"F2.wireOp",EDGE,"E18")])],"isStart":true}),makeQuery(id+"F3.opExtrude","CAP_FACE",FACE,{"disambiguationData":[OSD([subQ1,sQuery(id+"F2.wireOp",EDGE,"E19"),sQuery(id+"F2.wireOp",EDGE,"E20"),sQuery(id+"F2.wireOp",EDGE,"E21")])],"isStart":true}),makeQuery(id+"F3.opExtrude","CAP_FACE",FACE,{"disambiguationData":[OSD([subQ1,sQuery(id+"F2.wireOp",EDGE,"E22"),sQuery(id+"F2.wireOp",EDGE,"E23"),sQuery(id+"F2.wireOp",EDGE,"E24")])],"isStart":true}),makeQuery(id+"F3.opExtrude","CAP_FACE",FACE,{"disambiguationData":[OSD([subQ1,sQuery(id+"F2.wireOp",EDGE,"E25"),sQuery(id+"F2.wireOp",EDGE,"E26"),sQuery(id+"F2.wireOp",EDGE,"E27")])],"isStart":true}),makeQuery(id+"F3.opExtrude","CAP_FACE",FACE,{"disambiguationData":[OSD([subQ1,sQuery(id+"F2.wireOp",EDGE,"E28"),sQuery(id+"F2.wireOp",EDGE,"E29"),sQuery(id+"F2.wireOp",EDGE,"E30")])],"isStart":true}),makeQuery(id+"F3.opExtrude","CAP_FACE",FACE,{"disambiguationData":[OSD([subQ0,sQuery(id+"F2.wireOp",EDGE,"E31.MirrorCS"),sQuery(id+"F2.wireOp",EDGE,"E33.MirrorCS"),sQuery(id+"F2.wireOp",EDGE,"E48.MirrorCS")])],"isStart":true}),makeQuery(id+"F3.opExtrude","CAP_FACE",FACE,{"disambiguationData":[OSD([subQ0,sQuery(id+"F2.wireOp",EDGE,"E32.MirrorCS"),sQuery(id+"F2.wireOp",EDGE,"E46.MirrorCS"),sQuery(id+"F2.wireOp",EDGE,"E49.MirrorCS")])],"isStart":true}),makeQuery(id+"F3.opExtrude","CAP_FACE",FACE,{"disambiguationData":[OSD([subQ0,sQuery(id+"F2.wireOp",EDGE,"E34.MirrorCS"),sQuery(id+"F2.wireOp",EDGE,"E45.MirrorCS"),sQuery(id+"F2.wireOp",EDGE,"E50.MirrorCS")])],"isStart":true}),makeQuery(id+"F3.opExtrude","CAP_FACE",FACE,{"disambiguationData":[OSD([subQ0,sQuery(id+"F2.wireOp",EDGE,"E35.MirrorCS"),sQuery(id+"F2.wireOp",EDGE,"E36.MirrorCS"),sQuery(id+"F2.wireOp",EDGE,"E38.MirrorCS")])],"isStart":true}),makeQuery(id+"F3.opExtrude","CAP_FACE",FACE,{"disambiguationData":[OSD([subQ0,sQuery(id+"F2.wireOp",EDGE,"E37.MirrorCS"),sQuery(id+"F2.wireOp",EDGE,"E39.MirrorCS"),sQuery(id+"F2.wireOp",EDGE,"E43.MirrorCS")])],"isStart":true}),makeQuery(id+"F3.opExtrude","CAP_FACE",FACE,{"disambiguationData":[OSD([subQ0,sQuery(id+"F2.wireOp",EDGE,"E40.MirrorCS"),sQuery(id+"F2.wireOp",EDGE,"E44.MirrorCS"),sQuery(id+"F2.wireOp",EDGE,"E51.MirrorCS")])],"isStart":true}),makeQuery(id+"F3.opExtrude","CAP_FACE",FACE,{"disambiguationData":[OSD([subQ0,sQuery(id+"F2.wireOp",EDGE,"E41.MirrorCS"),sQuery(id+"F2.wireOp",EDGE,"E42.MirrorCS"),sQuery(id+"F2.wireOp",EDGE,"E47.MirrorCS")])],"isStart":true})]});}
            var sketch = newSketch(context, id + "F14", { "sketchPlane" : qUnion([Q0])});
            skLineSegment(sketch, "E58", {"start": v(-163.1, 234) * mm, "end": v(-137.97, 234) * mm});
            skLineSegment(sketch, "E59", {"start": v(-137.97, 234) * mm, "end": v(-128.8, 244) * mm});
            skCircle(sketch, "E60", {"center": v(-139.84, 238.25) * mm, "radius": 4.25 * mm, "construction": true});
            skLineSegment(sketch, "E61", {"start": v(0, 0) * mm, "end": v(0, 244) * mm, "construction": true});
            skLineSegment(sketch, "E62.MirrorCS", {"start": v(163.1, 234) * mm, "end": v(137.97, 234) * mm});
            skLineSegment(sketch, "E63.MirrorCS", {"start": v(137.97, 234) * mm, "end": v(128.8, 244) * mm});
            skCircle(sketch, "E64.MirrorC", {"center": v(139.84, 238.25) * mm, "radius": 4.25 * mm, "construction": true});
            skSolve(sketch);
        }
        {
            var Q0;
            {var subQ0=sQuery(id+"F14.wireOp",EDGE,"E58");Q0=makeQuery(id+"F14.imprint","IMPRINT",FACE,{"disambiguationData":[TD([[makeQuery(id+"F14.imprint","IMPRINT",EDGE,{"derivedFrom":subQ0}),1.0]])]});}
            var Q1;
            {var subQ0=sQuery(id+"F14.wireOp",EDGE,"E62.MirrorCS");Q1=makeQuery(id+"F14.imprint","IMPRINT",FACE,{"disambiguationData":[TD([[makeQuery(id+"F14.imprint","IMPRINT",EDGE,{"derivedFrom":subQ0}),-1.0]])]});}
            extrude(context, id + "F15", {"entities" : qUnion([Q0, Q1]), "operationType" : NewBodyOperationType.REMOVE, "oppositeDirection" : true, "depth" : 25 * mm});
        }
        {
            var Q0;
            Q0=makeQuery(id+"F15.boolean.opBoolean","COPY",EDGE,{"derivedFrom":makeQuery(id+"F15.opExtrude","SWEPT_EDGE",EDGE,{"disambiguationData":[OSD([sQuery(id+"F14.wireOp",EDGE,"E58"),sQuery(id+"F14.wireOp",EDGE,"E59")])]})});
            var Q1;
            Q1=makeQuery(id+"F15.boolean.opBoolean","COPY",EDGE,{"derivedFrom":makeQuery(id+"F15.opExtrude","SWEPT_EDGE",EDGE,{"disambiguationData":[OSD([sQuery(id+"F0.wireOp",EDGE,"E0.bottom"),sQuery(id+"F14.wireOp",EDGE,"E59")])]})});
            var Q2;
            Q2=makeQuery(id+"F15.boolean.opBoolean","COPY",EDGE,{"derivedFrom":makeQuery(id+"F15.opExtrude","SWEPT_EDGE",EDGE,{"disambiguationData":[OSD([sQuery(id+"F0.wireOp",EDGE,"E0.bottom"),sQuery(id+"F14.wireOp",EDGE,"E63.MirrorCS")])]})});
            var Q3;
            Q3=makeQuery(id+"F15.boolean.opBoolean","COPY",EDGE,{"derivedFrom":makeQuery(id+"F15.opExtrude","SWEPT_EDGE",EDGE,{"disambiguationData":[OSD([sQuery(id+"F14.wireOp",EDGE,"E62.MirrorCS"),sQuery(id+"F14.wireOp",EDGE,"E63.MirrorCS")])]})});
            fillet(context, id + "F16", {"entities" : qUnion([Q0, Q1, Q2, Q3]), "radius" : 8.5 * mm, "tangentPropagation" : true, "allowEdgeOverflow" : false});
        }
        {
            var Q0;
            Q0=makeQuery(id+"F15.boolean.opBoolean","COPY",EDGE,{"derivedFrom":makeQuery(id+"F15.opExtrude","CAP_EDGE",EDGE,{"disambiguationData":[OSD([sQuery(id+"F14.wireOp",EDGE,"E58")])],"isStart":true})});
            var Q1;
            {var subQ0=sQuery(id+"F0.wireOp",EDGE,"E0.left");var subQ1=sQuery(id+"F0.wireOp",EDGE,"E0.right");Q1=makeQuery(id+"F15.boolean.opBoolean","INTERSECT",EDGE,{"derivedFrom":[makeQuery(id+"F3.boolean.opBoolean","MERGE",FACE,{"derivedFrom":[makeQuery(id+"F1.opExtrude","CAP_FACE",FACE,{"disambiguationData":[OSD([sQuery(id+"F0.wireOp",EDGE,"E0.bottom"),sQuery(id+"F0.wireOp",EDGE,"E0.top"),subQ0,subQ1])],"isStart":true}),makeQuery(id+"F3.opExtrude","CAP_FACE",FACE,{"disambiguationData":[OSD([subQ1,sQuery(id+"F2.wireOp",EDGE,"E1"),sQuery(id+"F2.wireOp",EDGE,"E2"),sQuery(id+"F2.wireOp",EDGE,"E4.MirrorCS")])],"isStart":false}),makeQuery(id+"F3.opExtrude","CAP_FACE",FACE,{"disambiguationData":[OSD([subQ0,sQuery(id+"F2.wireOp",EDGE,"E6.MirrorCS"),sQuery(id+"F2.wireOp",EDGE,"E8.MirrorCS"),sQuery(id+"F2.wireOp",EDGE,"E9.MirrorCS")])],"isStart":false}),makeQuery(id+"F3.opExtrude","CAP_FACE",FACE,{"disambiguationData":[OSD([subQ1,sQuery(id+"F2.wireOp",EDGE,"E10"),sQuery(id+"F2.wireOp",EDGE,"E11"),sQuery(id+"F2.wireOp",EDGE,"E12")])],"isStart":false}),makeQuery(id+"F3.opExtrude","CAP_FACE",FACE,{"disambiguationData":[OSD([subQ1,sQuery(id+"F2.wireOp",EDGE,"E13"),sQuery(id+"F2.wireOp",EDGE,"E14"),sQuery(id+"F2.wireOp",EDGE,"E15")])],"isStart":false}),makeQuery(id+"F3.opExtrude","CAP_FACE",FACE,{"disambiguationData":[OSD([subQ1,sQuery(id+"F2.wireOp",EDGE,"E16"),sQuery(id+"F2.wireOp",EDGE,"E17"),sQuery(id+"F2.wireOp",EDGE,"E18")])],"isStart":false}),makeQuery(id+"F3.opExtrude","CAP_FACE",FACE,{"disambiguationData":[OSD([subQ1,sQuery(id+"F2.wireOp",EDGE,"E19"),sQuery(id+"F2.wireOp",EDGE,"E20"),sQuery(id+"F2.wireOp",EDGE,"E21")])],"isStart":false}),makeQuery(id+"F3.opExtrude","CAP_FACE",FACE,{"disambiguationData":[OSD([subQ1,sQuery(id+"F2.wireOp",EDGE,"E22"),sQuery(id+"F2.wireOp",EDGE,"E23"),sQuery(id+"F2.wireOp",EDGE,"E24")])],"isStart":false}),makeQuery(id+"F3.opExtrude","CAP_FACE",FACE,{"disambiguationData":[OSD([subQ1,sQuery(id+"F2.wireOp",EDGE,"E25"),sQuery(id+"F2.wireOp",EDGE,"E26"),sQuery(id+"F2.wireOp",EDGE,"E27")])],"isStart":false}),makeQuery(id+"F3.opExtrude","CAP_FACE",FACE,{"disambiguationData":[OSD([subQ1,sQuery(id+"F2.wireOp",EDGE,"E28"),sQuery(id+"F2.wireOp",EDGE,"E29"),sQuery(id+"F2.wireOp",EDGE,"E30")])],"isStart":false}),makeQuery(id+"F3.opExtrude","CAP_FACE",FACE,{"disambiguationData":[OSD([subQ0,sQuery(id+"F2.wireOp",EDGE,"E31.MirrorCS"),sQuery(id+"F2.wireOp",EDGE,"E33.MirrorCS"),sQuery(id+"F2.wireOp",EDGE,"E48.MirrorCS")])],"isStart":false}),makeQuery(id+"F3.opExtrude","CAP_FACE",FACE,{"disambiguationData":[OSD([subQ0,sQuery(id+"F2.wireOp",EDGE,"E32.MirrorCS"),sQuery(id+"F2.wireOp",EDGE,"E46.MirrorCS"),sQuery(id+"F2.wireOp",EDGE,"E49.MirrorCS")])],"isStart":false}),makeQuery(id+"F3.opExtrude","CAP_FACE",FACE,{"disambiguationData":[OSD([subQ0,sQuery(id+"F2.wireOp",EDGE,"E34.MirrorCS"),sQuery(id+"F2.wireOp",EDGE,"E45.MirrorCS"),sQuery(id+"F2.wireOp",EDGE,"E50.MirrorCS")])],"isStart":false}),makeQuery(id+"F3.opExtrude","CAP_FACE",FACE,{"disambiguationData":[OSD([subQ0,sQuery(id+"F2.wireOp",EDGE,"E35.MirrorCS"),sQuery(id+"F2.wireOp",EDGE,"E36.MirrorCS"),sQuery(id+"F2.wireOp",EDGE,"E38.MirrorCS")])],"isStart":false}),makeQuery(id+"F3.opExtrude","CAP_FACE",FACE,{"disambiguationData":[OSD([subQ0,sQuery(id+"F2.wireOp",EDGE,"E37.MirrorCS"),sQuery(id+"F2.wireOp",EDGE,"E39.MirrorCS"),sQuery(id+"F2.wireOp",EDGE,"E43.MirrorCS")])],"isStart":false}),makeQuery(id+"F3.opExtrude","CAP_FACE",FACE,{"disambiguationData":[OSD([subQ0,sQuery(id+"F2.wireOp",EDGE,"E40.MirrorCS"),sQuery(id+"F2.wireOp",EDGE,"E44.MirrorCS"),sQuery(id+"F2.wireOp",EDGE,"E51.MirrorCS")])],"isStart":false}),makeQuery(id+"F3.opExtrude","CAP_FACE",FACE,{"disambiguationData":[OSD([subQ0,sQuery(id+"F2.wireOp",EDGE,"E41.MirrorCS"),sQuery(id+"F2.wireOp",EDGE,"E42.MirrorCS"),sQuery(id+"F2.wireOp",EDGE,"E47.MirrorCS")])],"isStart":false})]}),makeQuery(id+"F15.opExtrude","SWEPT_FACE",FACE,{"disambiguationData":[OSD([sQuery(id+"F14.wireOp",EDGE,"E58")])]})]});}
            chamfer(context, id + "F17", {"entities" : qUnion([Q0, Q1]), "width" : .5 * mm, "tangentPropagation" : true});
        }
        {
            var Q0;
            {var subQ0=sQuery(id+"F0.wireOp",EDGE,"E0.left");var subQ1=sQuery(id+"F0.wireOp",EDGE,"E0.right");Q0=makeQuery(id+"F3.boolean.opBoolean","MERGE",FACE,{"derivedFrom":[makeQuery(id+"F1.opExtrude","CAP_FACE",FACE,{"disambiguationData":[OSD([sQuery(id+"F0.wireOp",EDGE,"E0.bottom"),sQuery(id+"F0.wireOp",EDGE,"E0.top"),subQ0,subQ1])],"isStart":true}),makeQuery(id+"F3.opExtrude","CAP_FACE",FACE,{"disambiguationData":[OSD([subQ1,sQuery(id+"F2.wireOp",EDGE,"E1"),sQuery(id+"F2.wireOp",EDGE,"E2"),sQuery(id+"F2.wireOp",EDGE,"E4.MirrorCS")])],"isStart":false}),makeQuery(id+"F3.opExtrude","CAP_FACE",FACE,{"disambiguationData":[OSD([subQ0,sQuery(id+"F2.wireOp",EDGE,"E6.MirrorCS"),sQuery(id+"F2.wireOp",EDGE,"E8.MirrorCS"),sQuery(id+"F2.wireOp",EDGE,"E9.MirrorCS")])],"isStart":false}),makeQuery(id+"F3.opExtrude","CAP_FACE",FACE,{"disambiguationData":[OSD([subQ1,sQuery(id+"F2.wireOp",EDGE,"E10"),sQuery(id+"F2.wireOp",EDGE,"E11"),sQuery(id+"F2.wireOp",EDGE,"E12")])],"isStart":false}),makeQuery(id+"F3.opExtrude","CAP_FACE",FACE,{"disambiguationData":[OSD([subQ1,sQuery(id+"F2.wireOp",EDGE,"E13"),sQuery(id+"F2.wireOp",EDGE,"E14"),sQuery(id+"F2.wireOp",EDGE,"E15")])],"isStart":false}),makeQuery(id+"F3.opExtrude","CAP_FACE",FACE,{"disambiguationData":[OSD([subQ1,sQuery(id+"F2.wireOp",EDGE,"E16"),sQuery(id+"F2.wireOp",EDGE,"E17"),sQuery(id+"F2.wireOp",EDGE,"E18")])],"isStart":false}),makeQuery(id+"F3.opExtrude","CAP_FACE",FACE,{"disambiguationData":[OSD([subQ1,sQuery(id+"F2.wireOp",EDGE,"E19"),sQuery(id+"F2.wireOp",EDGE,"E20"),sQuery(id+"F2.wireOp",EDGE,"E21")])],"isStart":false}),makeQuery(id+"F3.opExtrude","CAP_FACE",FACE,{"disambiguationData":[OSD([subQ1,sQuery(id+"F2.wireOp",EDGE,"E22"),sQuery(id+"F2.wireOp",EDGE,"E23"),sQuery(id+"F2.wireOp",EDGE,"E24")])],"isStart":false}),makeQuery(id+"F3.opExtrude","CAP_FACE",FACE,{"disambiguationData":[OSD([subQ1,sQuery(id+"F2.wireOp",EDGE,"E25"),sQuery(id+"F2.wireOp",EDGE,"E26"),sQuery(id+"F2.wireOp",EDGE,"E27")])],"isStart":false}),makeQuery(id+"F3.opExtrude","CAP_FACE",FACE,{"disambiguationData":[OSD([subQ1,sQuery(id+"F2.wireOp",EDGE,"E28"),sQuery(id+"F2.wireOp",EDGE,"E29"),sQuery(id+"F2.wireOp",EDGE,"E30")])],"isStart":false}),makeQuery(id+"F3.opExtrude","CAP_FACE",FACE,{"disambiguationData":[OSD([subQ0,sQuery(id+"F2.wireOp",EDGE,"E31.MirrorCS"),sQuery(id+"F2.wireOp",EDGE,"E33.MirrorCS"),sQuery(id+"F2.wireOp",EDGE,"E48.MirrorCS")])],"isStart":false}),makeQuery(id+"F3.opExtrude","CAP_FACE",FACE,{"disambiguationData":[OSD([subQ0,sQuery(id+"F2.wireOp",EDGE,"E32.MirrorCS"),sQuery(id+"F2.wireOp",EDGE,"E46.MirrorCS"),sQuery(id+"F2.wireOp",EDGE,"E49.MirrorCS")])],"isStart":false}),makeQuery(id+"F3.opExtrude","CAP_FACE",FACE,{"disambiguationData":[OSD([subQ0,sQuery(id+"F2.wireOp",EDGE,"E34.MirrorCS"),sQuery(id+"F2.wireOp",EDGE,"E45.MirrorCS"),sQuery(id+"F2.wireOp",EDGE,"E50.MirrorCS")])],"isStart":false}),makeQuery(id+"F3.opExtrude","CAP_FACE",FACE,{"disambiguationData":[OSD([subQ0,sQuery(id+"F2.wireOp",EDGE,"E35.MirrorCS"),sQuery(id+"F2.wireOp",EDGE,"E36.MirrorCS"),sQuery(id+"F2.wireOp",EDGE,"E38.MirrorCS")])],"isStart":false}),makeQuery(id+"F3.opExtrude","CAP_FACE",FACE,{"disambiguationData":[OSD([subQ0,sQuery(id+"F2.wireOp",EDGE,"E37.MirrorCS"),sQuery(id+"F2.wireOp",EDGE,"E39.MirrorCS"),sQuery(id+"F2.wireOp",EDGE,"E43.MirrorCS")])],"isStart":false}),makeQuery(id+"F3.opExtrude","CAP_FACE",FACE,{"disambiguationData":[OSD([subQ0,sQuery(id+"F2.wireOp",EDGE,"E40.MirrorCS"),sQuery(id+"F2.wireOp",EDGE,"E44.MirrorCS"),sQuery(id+"F2.wireOp",EDGE,"E51.MirrorCS")])],"isStart":false}),makeQuery(id+"F3.opExtrude","CAP_FACE",FACE,{"disambiguationData":[OSD([subQ0,sQuery(id+"F2.wireOp",EDGE,"E41.MirrorCS"),sQuery(id+"F2.wireOp",EDGE,"E42.MirrorCS"),sQuery(id+"F2.wireOp",EDGE,"E47.MirrorCS")])],"isStart":false})]});}
            var sketch = newSketch(context, id + "F18", { "sketchPlane" : qUnion([Q0])});
            skLineSegment(sketch, "E65.bottom", {"start": v(-163.1, -172.7) * mm, "end": v(-156.8, -172.7) * mm});
            skLineSegment(sketch, "E65.top", {"start": v(-163.1, -175.7) * mm, "end": v(-156.8, -175.7) * mm});
            skLineSegment(sketch, "E65.left", {"start": v(-163.1, -172.7) * mm, "end": v(-163.1, -175.7) * mm});
            skLineSegment(sketch, "E65.right", {"start": v(-153.1, -172.7) * mm, "end": v(-153.1, -175.7) * mm, "construction": true});
            skPoint(sketch, "E65.middle", {"position": v(-158.1, -174.2) * mm});
            skArc(sketch, "E66", {"start": v(-153.1, -175.7) * mm, "mid": v(-151.6, -174.2) * mm, "end": v(-153.1, -172.7) * mm});
            skLineSegment(sketch, "E67.bottom", {"start": v(-155.1, -170.85) * mm, "end": v(-156.8, -170.85) * mm, "construction": true});
            skLineSegment(sketch, "E67.top", {"start": v(-155.1, -177.55) * mm, "end": v(-156.8, -177.55) * mm, "construction": true});
            skLineSegment(sketch, "E67.left", {"start": v(-155.1, -170.85) * mm, "end": v(-155.1, -177.55) * mm});
            skLineSegment(sketch, "E67.right", {"start": v(-156.8, -170.85) * mm, "end": v(-156.8, -177.55) * mm});
            skPoint(sketch, "E67.middle", {"position": v(-155.95, -174.2) * mm});
            skArc(sketch, "E68", {"start": v(-156.8, -176.7) * mm, "mid": v(-155.95, -177.55) * mm, "end": v(-155.1, -176.7) * mm});
            skArc(sketch, "E69", {"start": v(-155.1, -171.7) * mm, "mid": v(-155.95, -170.85) * mm, "end": v(-156.8, -171.7) * mm});
            skLineSegment(sketch, "E70.trimOffspring", {"start": v(-155.1, -172.7) * mm, "end": v(-153.1, -172.7) * mm});
            skLineSegment(sketch, "E71.trimOffspring", {"start": v(-155.1, -175.7) * mm, "end": v(-153.1, -175.7) * mm});
            skLineSegment(sketch, "E72.1.0.0", {"start": v(-156.8, -48.85) * mm, "end": v(-156.8, -55.55) * mm});
            skArc(sketch, "E72.1.0.1", {"start": v(-155.1, -49.7) * mm, "mid": v(-155.95, -48.85) * mm, "end": v(-156.8, -49.7) * mm});
            skLineSegment(sketch, "E72.1.0.2", {"start": v(-155.1, -48.85) * mm, "end": v(-155.1, -55.55) * mm});
            skLineSegment(sketch, "E72.1.0.3", {"start": v(-163.1, -50.7) * mm, "end": v(-163.1, -53.7) * mm});
            skPoint(sketch, "E72.1.0.4", {"position": v(-158.1, -52.2) * mm});
            skLineSegment(sketch, "E72.1.0.5", {"start": v(-153.1, -50.7) * mm, "end": v(-153.1, -53.7) * mm, "construction": true});
            skArc(sketch, "E72.1.0.6", {"start": v(-156.8, -54.7) * mm, "mid": v(-155.95, -55.55) * mm, "end": v(-155.1, -54.7) * mm});
            skLineSegment(sketch, "E72.1.0.7", {"start": v(-163.1, -50.7) * mm, "end": v(-156.8, -50.7) * mm});
            skLineSegment(sketch, "E72.1.0.8", {"start": v(-163.1, -53.7) * mm, "end": v(-156.8, -53.7) * mm});
            skArc(sketch, "E72.1.0.9", {"start": v(-153.1, -53.7) * mm, "mid": v(-151.6, -52.2) * mm, "end": v(-153.1, -50.7) * mm});
            skLineSegment(sketch, "E72.1.0.10", {"start": v(-155.1, -48.85) * mm, "end": v(-156.8, -48.85) * mm, "construction": true});
            skLineSegment(sketch, "E72.1.0.11", {"start": v(-155.1, -55.55) * mm, "end": v(-156.8, -55.55) * mm, "construction": true});
            skPoint(sketch, "E72.1.0.12", {"position": v(-155.95, -52.2) * mm});
            skLineSegment(sketch, "E72.1.0.13", {"start": v(-155.1, -50.7) * mm, "end": v(-153.1, -50.7) * mm});
            skLineSegment(sketch, "E72.1.0.14", {"start": v(-155.1, -53.7) * mm, "end": v(-153.1, -53.7) * mm});
            skLineSegment(sketch, "E72.2.0.0", {"start": v(-156.8, 73.15) * mm, "end": v(-156.8, 66.45) * mm});
            skArc(sketch, "E72.2.0.1", {"start": v(-155.1, 72.3) * mm, "mid": v(-155.95, 73.15) * mm, "end": v(-156.8, 72.3) * mm});
            skLineSegment(sketch, "E72.2.0.2", {"start": v(-155.1, 73.15) * mm, "end": v(-155.1, 66.45) * mm});
            skLineSegment(sketch, "E72.2.0.3", {"start": v(-163.1, 71.3) * mm, "end": v(-163.1, 68.3) * mm});
            skPoint(sketch, "E72.2.0.4", {"position": v(-158.1, 69.8) * mm});
            skLineSegment(sketch, "E72.2.0.5", {"start": v(-153.1, 71.3) * mm, "end": v(-153.1, 68.3) * mm, "construction": true});
            skArc(sketch, "E72.2.0.6", {"start": v(-156.8, 67.3) * mm, "mid": v(-155.95, 66.45) * mm, "end": v(-155.1, 67.3) * mm});
            skLineSegment(sketch, "E72.2.0.7", {"start": v(-163.1, 71.3) * mm, "end": v(-156.8, 71.3) * mm});
            skLineSegment(sketch, "E72.2.0.8", {"start": v(-163.1, 68.3) * mm, "end": v(-156.8, 68.3) * mm});
            skArc(sketch, "E72.2.0.9", {"start": v(-153.1, 68.3) * mm, "mid": v(-151.6, 69.8) * mm, "end": v(-153.1, 71.3) * mm});
            skLineSegment(sketch, "E72.2.0.10", {"start": v(-155.1, 73.15) * mm, "end": v(-156.8, 73.15) * mm, "construction": true});
            skLineSegment(sketch, "E72.2.0.11", {"start": v(-155.1, 66.45) * mm, "end": v(-156.8, 66.45) * mm, "construction": true});
            skPoint(sketch, "E72.2.0.12", {"position": v(-155.95, 69.8) * mm});
            skLineSegment(sketch, "E72.2.0.13", {"start": v(-155.1, 71.3) * mm, "end": v(-153.1, 71.3) * mm});
            skLineSegment(sketch, "E72.2.0.14", {"start": v(-155.1, 68.3) * mm, "end": v(-153.1, 68.3) * mm});
            skLineSegment(sketch, "E72.3.0.0", {"start": v(-156.8, 195.15) * mm, "end": v(-156.8, 188.45) * mm});
            skArc(sketch, "E72.3.0.1", {"start": v(-155.1, 194.3) * mm, "mid": v(-155.95, 195.15) * mm, "end": v(-156.8, 194.3) * mm});
            skLineSegment(sketch, "E72.3.0.2", {"start": v(-155.1, 195.15) * mm, "end": v(-155.1, 188.45) * mm});
            skLineSegment(sketch, "E72.3.0.3", {"start": v(-163.1, 193.3) * mm, "end": v(-163.1, 190.3) * mm});
            skPoint(sketch, "E72.3.0.4", {"position": v(-158.1, 191.8) * mm});
            skLineSegment(sketch, "E72.3.0.5", {"start": v(-153.1, 193.3) * mm, "end": v(-153.1, 190.3) * mm, "construction": true});
            skArc(sketch, "E72.3.0.6", {"start": v(-156.8, 189.3) * mm, "mid": v(-155.95, 188.45) * mm, "end": v(-155.1, 189.3) * mm});
            skLineSegment(sketch, "E72.3.0.7", {"start": v(-163.1, 193.3) * mm, "end": v(-156.8, 193.3) * mm});
            skLineSegment(sketch, "E72.3.0.8", {"start": v(-163.1, 190.3) * mm, "end": v(-156.8, 190.3) * mm});
            skArc(sketch, "E72.3.0.9", {"start": v(-153.1, 190.3) * mm, "mid": v(-151.6, 191.8) * mm, "end": v(-153.1, 193.3) * mm});
            skLineSegment(sketch, "E72.3.0.10", {"start": v(-155.1, 195.15) * mm, "end": v(-156.8, 195.15) * mm, "construction": true});
            skLineSegment(sketch, "E72.3.0.11", {"start": v(-155.1, 188.45) * mm, "end": v(-156.8, 188.45) * mm, "construction": true});
            skPoint(sketch, "E72.3.0.12", {"position": v(-155.95, 191.8) * mm});
            skLineSegment(sketch, "E72.3.0.13", {"start": v(-155.1, 193.3) * mm, "end": v(-153.1, 193.3) * mm});
            skLineSegment(sketch, "E72.3.0.14", {"start": v(-155.1, 190.3) * mm, "end": v(-153.1, 190.3) * mm});
            skLineSegment(sketch, "E72.direction1", {"start": v(-163.1, -175.7) * mm, "end": v(-163.1, -53.7) * mm, "construction": true});
            skLineSegment(sketch, "E73.MirrorCS", {"start": v(155.1, -172.7) * mm, "end": v(153.1, -172.7) * mm});
            skArc(sketch, "E74.MirrorCS", {"start": v(156.8, -54.7) * mm, "mid": v(155.95, -55.55) * mm, "end": v(155.1, -54.7) * mm});
            skLineSegment(sketch, "E75.MirrorCS", {"start": v(155.1, -50.7) * mm, "end": v(153.1, -50.7) * mm});
            skArc(sketch, "E76.MirrorCS", {"start": v(155.1, 194.3) * mm, "mid": v(155.95, 195.15) * mm, "end": v(156.8, 194.3) * mm});
            skLineSegment(sketch, "E77.MirrorCS", {"start": v(155.1, -175.7) * mm, "end": v(153.1, -175.7) * mm});
            skArc(sketch, "E78.MirrorCS", {"start": v(155.1, -171.7) * mm, "mid": v(155.95, -170.85) * mm, "end": v(156.8, -171.7) * mm});
            skArc(sketch, "E79.MirrorCS", {"start": v(156.8, -176.7) * mm, "mid": v(155.95, -177.55) * mm, "end": v(155.1, -176.7) * mm});
            skLineSegment(sketch, "E80.MirrorCS", {"start": v(156.8, -170.85) * mm, "end": v(156.8, -177.55) * mm});
            skLineSegment(sketch, "E81.MirrorCS", {"start": v(155.1, -170.85) * mm, "end": v(155.1, -177.55) * mm});
            skLineSegment(sketch, "E82.MirrorCS", {"start": v(155.1, -170.85) * mm, "end": v(156.8, -170.85) * mm, "construction": true});
            skArc(sketch, "E83.MirrorCS", {"start": v(153.1, -175.7) * mm, "mid": v(151.6, -174.2) * mm, "end": v(153.1, -172.7) * mm});
            skLineSegment(sketch, "E84.MirrorCS", {"start": v(153.1, -172.7) * mm, "end": v(153.1, -175.7) * mm, "construction": true});
            skArc(sketch, "E85.MirrorCS", {"start": v(156.8, 67.3) * mm, "mid": v(155.95, 66.45) * mm, "end": v(155.1, 67.3) * mm});
            skLineSegment(sketch, "E86.MirrorCS", {"start": v(155.1, -53.7) * mm, "end": v(153.1, -53.7) * mm});
            skLineSegment(sketch, "E87.MirrorCS", {"start": v(155.1, 195.15) * mm, "end": v(155.1, 188.45) * mm});
            skArc(sketch, "E88.MirrorCS", {"start": v(153.1, 68.3) * mm, "mid": v(151.6, 69.8) * mm, "end": v(153.1, 71.3) * mm});
            skLineSegment(sketch, "E89.MirrorCS", {"start": v(155.1, 193.3) * mm, "end": v(153.1, 193.3) * mm});
            skLineSegment(sketch, "E90.MirrorCS", {"start": v(153.1, -50.7) * mm, "end": v(153.1, -53.7) * mm, "construction": true});
            skLineSegment(sketch, "E91.MirrorCS", {"start": v(155.1, 188.45) * mm, "end": v(156.8, 188.45) * mm, "construction": true});
            skLineSegment(sketch, "E92.MirrorCS", {"start": v(155.1, -55.55) * mm, "end": v(156.8, -55.55) * mm, "construction": true});
            skLineSegment(sketch, "E93.MirrorCS", {"start": v(156.8, 195.15) * mm, "end": v(156.8, 188.45) * mm});
            skLineSegment(sketch, "E94.MirrorCS", {"start": v(155.1, 195.15) * mm, "end": v(156.8, 195.15) * mm, "construction": true});
            skLineSegment(sketch, "E95.MirrorCS", {"start": v(155.1, -177.55) * mm, "end": v(156.8, -177.55) * mm, "construction": true});
            skLineSegment(sketch, "E96.MirrorCS", {"start": v(163.1, -175.7) * mm, "end": v(156.8, -175.7) * mm});
            skLineSegment(sketch, "E97.MirrorCS", {"start": v(163.1, -172.7) * mm, "end": v(156.8, -172.7) * mm});
            skLineSegment(sketch, "E98.MirrorCS", {"start": v(155.1, -48.85) * mm, "end": v(155.1, -55.55) * mm});
            skArc(sketch, "E99.MirrorCS", {"start": v(155.1, -49.7) * mm, "mid": v(155.95, -48.85) * mm, "end": v(156.8, -49.7) * mm});
            skLineSegment(sketch, "E100.MirrorCS", {"start": v(156.8, -48.85) * mm, "end": v(156.8, -55.55) * mm});
            skLineSegment(sketch, "E101.MirrorCS", {"start": v(155.1, -48.85) * mm, "end": v(156.8, -48.85) * mm, "construction": true});
            skLineSegment(sketch, "E102.MirrorCS", {"start": v(155.1, 73.15) * mm, "end": v(156.8, 73.15) * mm, "construction": true});
            skLineSegment(sketch, "E103.MirrorCS", {"start": v(163.1, -50.7) * mm, "end": v(156.8, -50.7) * mm});
            skLineSegment(sketch, "E104.MirrorCS", {"start": v(153.1, 71.3) * mm, "end": v(153.1, 68.3) * mm, "construction": true});
            skLineSegment(sketch, "E105.MirrorCS", {"start": v(155.1, 71.3) * mm, "end": v(153.1, 71.3) * mm});
            skLineSegment(sketch, "E106.MirrorCS", {"start": v(155.1, 73.15) * mm, "end": v(155.1, 66.45) * mm});
            skLineSegment(sketch, "E107.MirrorCS", {"start": v(155.1, 68.3) * mm, "end": v(153.1, 68.3) * mm});
            skArc(sketch, "E108.MirrorCS", {"start": v(153.1, 190.3) * mm, "mid": v(151.6, 191.8) * mm, "end": v(153.1, 193.3) * mm});
            skLineSegment(sketch, "E109.MirrorCS", {"start": v(155.1, 190.3) * mm, "end": v(153.1, 190.3) * mm});
            skLineSegment(sketch, "E110.MirrorCS", {"start": v(155.1, 66.45) * mm, "end": v(156.8, 66.45) * mm, "construction": true});
            skArc(sketch, "E111.MirrorCS", {"start": v(156.8, 189.3) * mm, "mid": v(155.95, 188.45) * mm, "end": v(155.1, 189.3) * mm});
            skArc(sketch, "E112.MirrorCS", {"start": v(155.1, 72.3) * mm, "mid": v(155.95, 73.15) * mm, "end": v(156.8, 72.3) * mm});
            skLineSegment(sketch, "E113.MirrorCS", {"start": v(153.1, 193.3) * mm, "end": v(153.1, 190.3) * mm, "construction": true});
            skArc(sketch, "E114.MirrorCS", {"start": v(153.1, -53.7) * mm, "mid": v(151.6, -52.2) * mm, "end": v(153.1, -50.7) * mm});
            skLineSegment(sketch, "E115.MirrorCS", {"start": v(156.8, 73.15) * mm, "end": v(156.8, 66.45) * mm});
            skLineSegment(sketch, "E116.MirrorCS", {"start": v(163.1, -50.7) * mm, "end": v(163.1, -53.7) * mm});
            skLineSegment(sketch, "E117.MirrorCS", {"start": v(163.1, -172.7) * mm, "end": v(163.1, -175.7) * mm});
            skLineSegment(sketch, "E118.MirrorCS", {"start": v(163.1, -53.7) * mm, "end": v(156.8, -53.7) * mm});
            skLineSegment(sketch, "E119.MirrorCS", {"start": v(163.1, 68.3) * mm, "end": v(156.8, 68.3) * mm});
            skLineSegment(sketch, "E120.MirrorCS", {"start": v(163.1, 71.3) * mm, "end": v(156.8, 71.3) * mm});
            skLineSegment(sketch, "E121.MirrorCS", {"start": v(163.1, 190.3) * mm, "end": v(156.8, 190.3) * mm});
            skLineSegment(sketch, "E122.MirrorCS", {"start": v(163.1, 193.3) * mm, "end": v(156.8, 193.3) * mm});
            skLineSegment(sketch, "E123.MirrorCS", {"start": v(163.1, 71.3) * mm, "end": v(163.1, 68.3) * mm});
            skLineSegment(sketch, "E124.MirrorCS", {"start": v(163.1, 193.3) * mm, "end": v(163.1, 190.3) * mm});
            skPoint(sketch, "E125.MirrorP", {"position": v(158.1, -174.2) * mm});
            skPoint(sketch, "E126.MirrorP", {"position": v(155.95, 69.8) * mm});
            skPoint(sketch, "E127.MirrorP", {"position": v(158.1, -52.2) * mm});
            skPoint(sketch, "E128.MirrorP", {"position": v(158.1, 191.8) * mm});
            skPoint(sketch, "E129.MirrorP", {"position": v(155.95, 191.8) * mm});
            skPoint(sketch, "E130.MirrorP", {"position": v(155.95, -52.2) * mm});
            skPoint(sketch, "E131.MirrorP", {"position": v(155.95, -174.2) * mm});
            skLineSegment(sketch, "E132.MirrorCS", {"start": v(163.1, -175.7) * mm, "end": v(163.1, -53.7) * mm, "construction": true});
            skPoint(sketch, "E133.MirrorP", {"position": v(158.1, 69.8) * mm});
            skSolve(sketch);
        }
        {
            var Q0;
            Q0=makeQuery(id+"F18.imprint","IMPRINT",FACE,{"disambiguationData":[TD([[makeQuery(id+"F18.imprint","IMPRINT",EDGE,{"derivedFrom":sQuery(id+"F18.wireOp",EDGE,"E72.3.0.3")}),1.0]])]});
            var Q1;
            Q1=makeQuery(id+"F18.imprint","IMPRINT",FACE,{"disambiguationData":[TD([[makeQuery(id+"F18.imprint","IMPRINT",EDGE,{"derivedFrom":sQuery(id+"F18.wireOp",EDGE,"E72.3.0.9")}),1.0]])]});
            var Q2;
            {var subQ0=sQuery(id+"F18.wireOp",EDGE,"E72.3.0.1");Q2=makeQuery(id+"F18.imprint","IMPRINT",FACE,{"disambiguationData":[TD([[makeQuery(id+"F18.imprint","IMPRINT",EDGE,{"derivedFrom":subQ0}),1.0]])]});}
            var Q3;
            Q3=makeQuery(id+"F18.imprint","IMPRINT",FACE,{"disambiguationData":[TD([[makeQuery(id+"F18.imprint","IMPRINT",EDGE,{"derivedFrom":sQuery(id+"F18.wireOp",EDGE,"E72.1.0.3")}),1.0]])]});
            var Q4;
            {var subQ0=sQuery(id+"F18.wireOp",EDGE,"E72.1.0.1");Q4=makeQuery(id+"F18.imprint","IMPRINT",FACE,{"disambiguationData":[TD([[makeQuery(id+"F18.imprint","IMPRINT",EDGE,{"derivedFrom":subQ0}),1.0]])]});}
            var Q5;
            Q5=makeQuery(id+"F18.imprint","IMPRINT",FACE,{"disambiguationData":[TD([[makeQuery(id+"F18.imprint","IMPRINT",EDGE,{"derivedFrom":sQuery(id+"F18.wireOp",EDGE,"E72.1.0.9")}),1.0]])]});
            var Q6;
            {var subQ0=sQuery(id+"F18.wireOp",EDGE,"E65.bottom");Q6=makeQuery(id+"F18.imprint","IMPRINT",FACE,{"disambiguationData":[TD([[makeQuery(id+"F18.imprint","IMPRINT",EDGE,{"derivedFrom":subQ0}),-1.0]])]});}
            var Q7;
            {var subQ3=sQuery(id+"F18.wireOp",EDGE,"E68");Q7=makeQuery(id+"F18.imprint","IMPRINT",FACE,{"disambiguationData":[TD([[makeQuery(id+"F18.imprint","IMPRINT",EDGE,{"derivedFrom":subQ3}),1.0]])]});}
            var Q8;
            Q8=makeQuery(id+"F18.imprint","IMPRINT",FACE,{"disambiguationData":[TD([[makeQuery(id+"F18.imprint","IMPRINT",EDGE,{"derivedFrom":sQuery(id+"F18.wireOp",EDGE,"E66")}),1.0]])]});
            var Q9;
            Q9=makeQuery(id+"F18.imprint","IMPRINT",FACE,{"disambiguationData":[TD([[makeQuery(id+"F18.imprint","IMPRINT",EDGE,{"derivedFrom":sQuery(id+"F18.wireOp",EDGE,"E72.2.0.3")}),1.0]])]});
            var Q10;
            {var subQ0=sQuery(id+"F18.wireOp",EDGE,"E72.2.0.1");Q10=makeQuery(id+"F18.imprint","IMPRINT",FACE,{"disambiguationData":[TD([[makeQuery(id+"F18.imprint","IMPRINT",EDGE,{"derivedFrom":subQ0}),1.0]])]});}
            var Q11;
            Q11=makeQuery(id+"F18.imprint","IMPRINT",FACE,{"disambiguationData":[TD([[makeQuery(id+"F18.imprint","IMPRINT",EDGE,{"derivedFrom":sQuery(id+"F18.wireOp",EDGE,"E72.2.0.9")}),1.0]])]});
            var Q12;
            {var subQ0=sQuery(id+"F18.wireOp",EDGE,"E96.MirrorCS");Q12=makeQuery(id+"F18.imprint","IMPRINT",FACE,{"disambiguationData":[TD([[makeQuery(id+"F18.imprint","IMPRINT",EDGE,{"derivedFrom":subQ0}),-1.0]])]});}
            var Q13;
            {var subQ0=sQuery(id+"F18.wireOp",EDGE,"E73.MirrorCS");Q13=makeQuery(id+"F18.imprint","IMPRINT",FACE,{"disambiguationData":[TD([[makeQuery(id+"F18.imprint","IMPRINT",EDGE,{"derivedFrom":subQ0}),1.0]])]});}
            var Q14;
            {var subQ3=sQuery(id+"F18.wireOp",EDGE,"E78.MirrorCS");Q14=makeQuery(id+"F18.imprint","IMPRINT",FACE,{"disambiguationData":[TD([[makeQuery(id+"F18.imprint","IMPRINT",EDGE,{"derivedFrom":subQ3}),-1.0]])]});}
            var Q15;
            {var subQ0=sQuery(id+"F18.wireOp",EDGE,"E75.MirrorCS");Q15=makeQuery(id+"F18.imprint","IMPRINT",FACE,{"disambiguationData":[TD([[makeQuery(id+"F18.imprint","IMPRINT",EDGE,{"derivedFrom":subQ0}),1.0]])]});}
            var Q16;
            {var subQ1=sQuery(id+"F18.wireOp",EDGE,"E74.MirrorCS");Q16=makeQuery(id+"F18.imprint","IMPRINT",FACE,{"disambiguationData":[TD([[makeQuery(id+"F18.imprint","IMPRINT",EDGE,{"derivedFrom":subQ1}),-1.0]])]});}
            var Q17;
            {var subQ0=sQuery(id+"F18.wireOp",EDGE,"E103.MirrorCS");Q17=makeQuery(id+"F18.imprint","IMPRINT",FACE,{"disambiguationData":[TD([[makeQuery(id+"F18.imprint","IMPRINT",EDGE,{"derivedFrom":subQ0}),1.0]])]});}
            var Q18;
            Q18=makeQuery(id+"F18.imprint","IMPRINT",FACE,{"disambiguationData":[TD([[makeQuery(id+"F18.imprint","IMPRINT",EDGE,{"derivedFrom":sQuery(id+"F18.wireOp",EDGE,"E88.MirrorCS")}),-1.0]])]});
            var Q19;
            {var subQ1=sQuery(id+"F18.wireOp",EDGE,"E85.MirrorCS");Q19=makeQuery(id+"F18.imprint","IMPRINT",FACE,{"disambiguationData":[TD([[makeQuery(id+"F18.imprint","IMPRINT",EDGE,{"derivedFrom":subQ1}),-1.0]])]});}
            var Q20;
            {var subQ0=sQuery(id+"F18.wireOp",EDGE,"E119.MirrorCS");Q20=makeQuery(id+"F18.imprint","IMPRINT",FACE,{"disambiguationData":[TD([[makeQuery(id+"F18.imprint","IMPRINT",EDGE,{"derivedFrom":subQ0}),-1.0]])]});}
            var Q21;
            {var subQ0=sQuery(id+"F18.wireOp",EDGE,"E89.MirrorCS");Q21=makeQuery(id+"F18.imprint","IMPRINT",FACE,{"disambiguationData":[TD([[makeQuery(id+"F18.imprint","IMPRINT",EDGE,{"derivedFrom":subQ0}),1.0]])]});}
            var Q22;
            {var subQ3=sQuery(id+"F18.wireOp",EDGE,"E76.MirrorCS");Q22=makeQuery(id+"F18.imprint","IMPRINT",FACE,{"disambiguationData":[TD([[makeQuery(id+"F18.imprint","IMPRINT",EDGE,{"derivedFrom":subQ3}),-1.0]])]});}
            var Q23;
            {var subQ0=sQuery(id+"F18.wireOp",EDGE,"E121.MirrorCS");Q23=makeQuery(id+"F18.imprint","IMPRINT",FACE,{"disambiguationData":[TD([[makeQuery(id+"F18.imprint","IMPRINT",EDGE,{"derivedFrom":subQ0}),-1.0]])]});}
            extrude(context, id + "F19", {"entities" : qUnion([Q0, Q1, Q2, Q3, Q4, Q5, Q6, Q7, Q8, Q9, Q10, Q11, Q12, Q13, Q14, Q15, Q16, Q17, Q18, Q19, Q20, Q21, Q22, Q23]), "operationType" : NewBodyOperationType.REMOVE, "oppositeDirection" : true, "depth" : 4.5 * mm});
        }
        {
            var Q0;
            {var subQ0=sQuery(id+"F0.wireOp",EDGE,"E0.left");var subQ1=sQuery(id+"F0.wireOp",EDGE,"E0.right");Q0=makeQuery(id+"F3.boolean.opBoolean","MERGE",FACE,{"derivedFrom":[makeQuery(id+"F1.opExtrude","CAP_FACE",FACE,{"disambiguationData":[OSD([sQuery(id+"F0.wireOp",EDGE,"E0.bottom"),sQuery(id+"F0.wireOp",EDGE,"E0.top"),subQ0,subQ1])],"isStart":true}),makeQuery(id+"F3.opExtrude","CAP_FACE",FACE,{"disambiguationData":[OSD([subQ1,sQuery(id+"F2.wireOp",EDGE,"E1"),sQuery(id+"F2.wireOp",EDGE,"E2"),sQuery(id+"F2.wireOp",EDGE,"E4.MirrorCS")])],"isStart":false}),makeQuery(id+"F3.opExtrude","CAP_FACE",FACE,{"disambiguationData":[OSD([subQ0,sQuery(id+"F2.wireOp",EDGE,"E6.MirrorCS"),sQuery(id+"F2.wireOp",EDGE,"E8.MirrorCS"),sQuery(id+"F2.wireOp",EDGE,"E9.MirrorCS")])],"isStart":false}),makeQuery(id+"F3.opExtrude","CAP_FACE",FACE,{"disambiguationData":[OSD([subQ1,sQuery(id+"F2.wireOp",EDGE,"E10"),sQuery(id+"F2.wireOp",EDGE,"E11"),sQuery(id+"F2.wireOp",EDGE,"E12")])],"isStart":false}),makeQuery(id+"F3.opExtrude","CAP_FACE",FACE,{"disambiguationData":[OSD([subQ1,sQuery(id+"F2.wireOp",EDGE,"E13"),sQuery(id+"F2.wireOp",EDGE,"E14"),sQuery(id+"F2.wireOp",EDGE,"E15")])],"isStart":false}),makeQuery(id+"F3.opExtrude","CAP_FACE",FACE,{"disambiguationData":[OSD([subQ1,sQuery(id+"F2.wireOp",EDGE,"E16"),sQuery(id+"F2.wireOp",EDGE,"E17"),sQuery(id+"F2.wireOp",EDGE,"E18")])],"isStart":false}),makeQuery(id+"F3.opExtrude","CAP_FACE",FACE,{"disambiguationData":[OSD([subQ1,sQuery(id+"F2.wireOp",EDGE,"E19"),sQuery(id+"F2.wireOp",EDGE,"E20"),sQuery(id+"F2.wireOp",EDGE,"E21")])],"isStart":false}),makeQuery(id+"F3.opExtrude","CAP_FACE",FACE,{"disambiguationData":[OSD([subQ1,sQuery(id+"F2.wireOp",EDGE,"E22"),sQuery(id+"F2.wireOp",EDGE,"E23"),sQuery(id+"F2.wireOp",EDGE,"E24")])],"isStart":false}),makeQuery(id+"F3.opExtrude","CAP_FACE",FACE,{"disambiguationData":[OSD([subQ1,sQuery(id+"F2.wireOp",EDGE,"E25"),sQuery(id+"F2.wireOp",EDGE,"E26"),sQuery(id+"F2.wireOp",EDGE,"E27")])],"isStart":false}),makeQuery(id+"F3.opExtrude","CAP_FACE",FACE,{"disambiguationData":[OSD([subQ1,sQuery(id+"F2.wireOp",EDGE,"E28"),sQuery(id+"F2.wireOp",EDGE,"E29"),sQuery(id+"F2.wireOp",EDGE,"E30")])],"isStart":false}),makeQuery(id+"F3.opExtrude","CAP_FACE",FACE,{"disambiguationData":[OSD([subQ0,sQuery(id+"F2.wireOp",EDGE,"E31.MirrorCS"),sQuery(id+"F2.wireOp",EDGE,"E33.MirrorCS"),sQuery(id+"F2.wireOp",EDGE,"E48.MirrorCS")])],"isStart":false}),makeQuery(id+"F3.opExtrude","CAP_FACE",FACE,{"disambiguationData":[OSD([subQ0,sQuery(id+"F2.wireOp",EDGE,"E32.MirrorCS"),sQuery(id+"F2.wireOp",EDGE,"E46.MirrorCS"),sQuery(id+"F2.wireOp",EDGE,"E49.MirrorCS")])],"isStart":false}),makeQuery(id+"F3.opExtrude","CAP_FACE",FACE,{"disambiguationData":[OSD([subQ0,sQuery(id+"F2.wireOp",EDGE,"E34.MirrorCS"),sQuery(id+"F2.wireOp",EDGE,"E45.MirrorCS"),sQuery(id+"F2.wireOp",EDGE,"E50.MirrorCS")])],"isStart":false}),makeQuery(id+"F3.opExtrude","CAP_FACE",FACE,{"disambiguationData":[OSD([subQ0,sQuery(id+"F2.wireOp",EDGE,"E35.MirrorCS"),sQuery(id+"F2.wireOp",EDGE,"E36.MirrorCS"),sQuery(id+"F2.wireOp",EDGE,"E38.MirrorCS")])],"isStart":false}),makeQuery(id+"F3.opExtrude","CAP_FACE",FACE,{"disambiguationData":[OSD([subQ0,sQuery(id+"F2.wireOp",EDGE,"E37.MirrorCS"),sQuery(id+"F2.wireOp",EDGE,"E39.MirrorCS"),sQuery(id+"F2.wireOp",EDGE,"E43.MirrorCS")])],"isStart":false}),makeQuery(id+"F3.opExtrude","CAP_FACE",FACE,{"disambiguationData":[OSD([subQ0,sQuery(id+"F2.wireOp",EDGE,"E40.MirrorCS"),sQuery(id+"F2.wireOp",EDGE,"E44.MirrorCS"),sQuery(id+"F2.wireOp",EDGE,"E51.MirrorCS")])],"isStart":false}),makeQuery(id+"F3.opExtrude","CAP_FACE",FACE,{"disambiguationData":[OSD([subQ0,sQuery(id+"F2.wireOp",EDGE,"E41.MirrorCS"),sQuery(id+"F2.wireOp",EDGE,"E42.MirrorCS"),sQuery(id+"F2.wireOp",EDGE,"E47.MirrorCS")])],"isStart":false})]});}
            var sketch = newSketch(context, id + "F20", { "sketchPlane" : qUnion([Q0])});
            skLineSegment(sketch, "E134.bottom", {"start": v(-133.7, -200.1) * mm, "end": v(-149.9, -200.1) * mm});
            skLineSegment(sketch, "E134.top", {"start": v(-133.7, -193.9) * mm, "end": v(-149.9, -193.9) * mm});
            skLineSegment(sketch, "E134.left", {"start": v(-133.7, -200.1) * mm, "end": v(-133.7, -193.9) * mm, "construction": true});
            skLineSegment(sketch, "E134.right", {"start": v(-149.9, -200.1) * mm, "end": v(-149.9, -193.9) * mm, "construction": true});
            skPoint(sketch, "E134.middle", {"position": v(-141.8, -197) * mm});
            skArc(sketch, "E135", {"start": v(-146.8, -193.9) * mm, "mid": v(-149.9, -197) * mm, "end": v(-146.8, -200.1) * mm});
            skArc(sketch, "E136", {"start": v(-136.8, -200.1) * mm, "mid": v(-133.7, -197) * mm, "end": v(-136.8, -193.9) * mm});
            skLineSegment(sketch, "E137.MirrorCS", {"start": v(133.7, -200.1) * mm, "end": v(149.9, -200.1) * mm});
            skLineSegment(sketch, "E138.MirrorCS", {"start": v(133.7, -193.9) * mm, "end": v(149.9, -193.9) * mm});
            skLineSegment(sketch, "E139.MirrorCS", {"start": v(149.9, -200.1) * mm, "end": v(149.9, -193.9) * mm, "construction": true});
            skLineSegment(sketch, "E140.MirrorCS", {"start": v(133.7, -200.1) * mm, "end": v(133.7, -193.9) * mm, "construction": true});
            skPoint(sketch, "E141.MirrorP", {"position": v(141.8, -197) * mm});
            skArc(sketch, "E142.MirrorCS", {"start": v(146.8, -193.9) * mm, "mid": v(149.9, -197) * mm, "end": v(146.8, -200.1) * mm});
            skArc(sketch, "E143.MirrorCS", {"start": v(136.8, -200.1) * mm, "mid": v(133.7, -197) * mm, "end": v(136.8, -193.9) * mm});
            skLineSegment(sketch, "E144.bottom", {"start": v(-83.65, 233.9) * mm, "end": v(-99.85, 233.9) * mm});
            skLineSegment(sketch, "E144.top", {"start": v(-83.65, 240.1) * mm, "end": v(-99.85, 240.1) * mm});
            skLineSegment(sketch, "E144.left", {"start": v(-83.65, 233.9) * mm, "end": v(-83.65, 240.1) * mm, "construction": true});
            skLineSegment(sketch, "E144.right", {"start": v(-99.85, 233.9) * mm, "end": v(-99.85, 240.1) * mm, "construction": true});
            skPoint(sketch, "E144.middle", {"position": v(-91.75, 237) * mm});
            skArc(sketch, "E145", {"start": v(-96.75, 240.1) * mm, "mid": v(-99.85, 237) * mm, "end": v(-96.75, 233.9) * mm});
            skArc(sketch, "E146", {"start": v(-86.75, 233.9) * mm, "mid": v(-83.65, 237) * mm, "end": v(-86.75, 240.1) * mm});
            skArc(sketch, "E147.MirrorCS", {"start": v(96.75, 240.1) * mm, "mid": v(99.85, 237) * mm, "end": v(96.75, 233.9) * mm});
            skLineSegment(sketch, "E148.MirrorCS", {"start": v(83.65, 233.9) * mm, "end": v(83.65, 240.1) * mm, "construction": true});
            skLineSegment(sketch, "E149.MirrorCS", {"start": v(99.85, 233.9) * mm, "end": v(99.85, 240.1) * mm, "construction": true});
            skArc(sketch, "E150.MirrorCS", {"start": v(86.75, 233.9) * mm, "mid": v(83.65, 237) * mm, "end": v(86.75, 240.1) * mm});
            skLineSegment(sketch, "E151.MirrorCS", {"start": v(83.65, 233.9) * mm, "end": v(99.85, 233.9) * mm});
            skLineSegment(sketch, "E152.MirrorCS", {"start": v(83.65, 240.1) * mm, "end": v(99.85, 240.1) * mm});
            skPoint(sketch, "E153.MirrorP", {"position": v(91.75, 237) * mm});
            skSolve(sketch);
        }
        {
            var Q0;
            {var subQ0=sQuery(id+"F20.wireOp",EDGE,"E145");Q0=makeQuery(id+"F20.imprint","IMPRINT",FACE,{"disambiguationData":[TD([[makeQuery(id+"F20.imprint","IMPRINT",EDGE,{"derivedFrom":subQ0}),1.0]])]});}
            var Q1;
            {var subQ0=sQuery(id+"F20.wireOp",EDGE,"E147.MirrorCS");Q1=makeQuery(id+"F20.imprint","IMPRINT",FACE,{"disambiguationData":[TD([[makeQuery(id+"F20.imprint","IMPRINT",EDGE,{"derivedFrom":subQ0}),-1.0]])]});}
            var Q2;
            {var subQ0=sQuery(id+"F20.wireOp",EDGE,"E135");Q2=makeQuery(id+"F20.imprint","IMPRINT",FACE,{"disambiguationData":[TD([[makeQuery(id+"F20.imprint","IMPRINT",EDGE,{"derivedFrom":subQ0}),1.0]])]});}
            var Q3;
            {var subQ0=sQuery(id+"F20.wireOp",EDGE,"E142.MirrorCS");Q3=makeQuery(id+"F20.imprint","IMPRINT",FACE,{"disambiguationData":[TD([[makeQuery(id+"F20.imprint","IMPRINT",EDGE,{"derivedFrom":subQ0}),-1.0]])]});}
            extrude(context, id + "F21", {"entities" : qUnion([Q0, Q1, Q2, Q3]), "operationType" : NewBodyOperationType.REMOVE, "oppositeDirection" : true, "depth" : 4.5 * mm});
        }
        {
            var Q0;
            {var subQ0=sQuery(id+"F0.wireOp",EDGE,"E0.left");var subQ1=sQuery(id+"F0.wireOp",EDGE,"E0.right");Q0=makeQuery(id+"F3.boolean.opBoolean","MERGE",FACE,{"derivedFrom":[makeQuery(id+"F1.opExtrude","CAP_FACE",FACE,{"disambiguationData":[OSD([sQuery(id+"F0.wireOp",EDGE,"E0.bottom"),sQuery(id+"F0.wireOp",EDGE,"E0.top"),subQ0,subQ1])],"isStart":true}),makeQuery(id+"F3.opExtrude","CAP_FACE",FACE,{"disambiguationData":[OSD([subQ1,sQuery(id+"F2.wireOp",EDGE,"E1"),sQuery(id+"F2.wireOp",EDGE,"E2"),sQuery(id+"F2.wireOp",EDGE,"E4.MirrorCS")])],"isStart":false}),makeQuery(id+"F3.opExtrude","CAP_FACE",FACE,{"disambiguationData":[OSD([subQ0,sQuery(id+"F2.wireOp",EDGE,"E6.MirrorCS"),sQuery(id+"F2.wireOp",EDGE,"E8.MirrorCS"),sQuery(id+"F2.wireOp",EDGE,"E9.MirrorCS")])],"isStart":false}),makeQuery(id+"F3.opExtrude","CAP_FACE",FACE,{"disambiguationData":[OSD([subQ1,sQuery(id+"F2.wireOp",EDGE,"E10"),sQuery(id+"F2.wireOp",EDGE,"E11"),sQuery(id+"F2.wireOp",EDGE,"E12")])],"isStart":false}),makeQuery(id+"F3.opExtrude","CAP_FACE",FACE,{"disambiguationData":[OSD([subQ1,sQuery(id+"F2.wireOp",EDGE,"E13"),sQuery(id+"F2.wireOp",EDGE,"E14"),sQuery(id+"F2.wireOp",EDGE,"E15")])],"isStart":false}),makeQuery(id+"F3.opExtrude","CAP_FACE",FACE,{"disambiguationData":[OSD([subQ1,sQuery(id+"F2.wireOp",EDGE,"E16"),sQuery(id+"F2.wireOp",EDGE,"E17"),sQuery(id+"F2.wireOp",EDGE,"E18")])],"isStart":false}),makeQuery(id+"F3.opExtrude","CAP_FACE",FACE,{"disambiguationData":[OSD([subQ1,sQuery(id+"F2.wireOp",EDGE,"E19"),sQuery(id+"F2.wireOp",EDGE,"E20"),sQuery(id+"F2.wireOp",EDGE,"E21")])],"isStart":false}),makeQuery(id+"F3.opExtrude","CAP_FACE",FACE,{"disambiguationData":[OSD([subQ1,sQuery(id+"F2.wireOp",EDGE,"E22"),sQuery(id+"F2.wireOp",EDGE,"E23"),sQuery(id+"F2.wireOp",EDGE,"E24")])],"isStart":false}),makeQuery(id+"F3.opExtrude","CAP_FACE",FACE,{"disambiguationData":[OSD([subQ1,sQuery(id+"F2.wireOp",EDGE,"E25"),sQuery(id+"F2.wireOp",EDGE,"E26"),sQuery(id+"F2.wireOp",EDGE,"E27")])],"isStart":false}),makeQuery(id+"F3.opExtrude","CAP_FACE",FACE,{"disambiguationData":[OSD([subQ1,sQuery(id+"F2.wireOp",EDGE,"E28"),sQuery(id+"F2.wireOp",EDGE,"E29"),sQuery(id+"F2.wireOp",EDGE,"E30")])],"isStart":false}),makeQuery(id+"F3.opExtrude","CAP_FACE",FACE,{"disambiguationData":[OSD([subQ0,sQuery(id+"F2.wireOp",EDGE,"E31.MirrorCS"),sQuery(id+"F2.wireOp",EDGE,"E33.MirrorCS"),sQuery(id+"F2.wireOp",EDGE,"E48.MirrorCS")])],"isStart":false}),makeQuery(id+"F3.opExtrude","CAP_FACE",FACE,{"disambiguationData":[OSD([subQ0,sQuery(id+"F2.wireOp",EDGE,"E32.MirrorCS"),sQuery(id+"F2.wireOp",EDGE,"E46.MirrorCS"),sQuery(id+"F2.wireOp",EDGE,"E49.MirrorCS")])],"isStart":false}),makeQuery(id+"F3.opExtrude","CAP_FACE",FACE,{"disambiguationData":[OSD([subQ0,sQuery(id+"F2.wireOp",EDGE,"E34.MirrorCS"),sQuery(id+"F2.wireOp",EDGE,"E45.MirrorCS"),sQuery(id+"F2.wireOp",EDGE,"E50.MirrorCS")])],"isStart":false}),makeQuery(id+"F3.opExtrude","CAP_FACE",FACE,{"disambiguationData":[OSD([subQ0,sQuery(id+"F2.wireOp",EDGE,"E35.MirrorCS"),sQuery(id+"F2.wireOp",EDGE,"E36.MirrorCS"),sQuery(id+"F2.wireOp",EDGE,"E38.MirrorCS")])],"isStart":false}),makeQuery(id+"F3.opExtrude","CAP_FACE",FACE,{"disambiguationData":[OSD([subQ0,sQuery(id+"F2.wireOp",EDGE,"E37.MirrorCS"),sQuery(id+"F2.wireOp",EDGE,"E39.MirrorCS"),sQuery(id+"F2.wireOp",EDGE,"E43.MirrorCS")])],"isStart":false}),makeQuery(id+"F3.opExtrude","CAP_FACE",FACE,{"disambiguationData":[OSD([subQ0,sQuery(id+"F2.wireOp",EDGE,"E40.MirrorCS"),sQuery(id+"F2.wireOp",EDGE,"E44.MirrorCS"),sQuery(id+"F2.wireOp",EDGE,"E51.MirrorCS")])],"isStart":false}),makeQuery(id+"F3.opExtrude","CAP_FACE",FACE,{"disambiguationData":[OSD([subQ0,sQuery(id+"F2.wireOp",EDGE,"E41.MirrorCS"),sQuery(id+"F2.wireOp",EDGE,"E42.MirrorCS"),sQuery(id+"F2.wireOp",EDGE,"E47.MirrorCS")])],"isStart":false})]});}
            var sketch = newSketch(context, id + "F22", { "sketchPlane" : qUnion([Q0])});
            skLineSegment(sketch, "E154.bottom", {"start": v(-26.1, 233.9) * mm, "end": v(-9.9, 233.9) * mm});
            skLineSegment(sketch, "E154.top", {"start": v(-26.1, 240.1) * mm, "end": v(-9.9, 240.1) * mm});
            skLineSegment(sketch, "E154.left", {"start": v(-26.1, 233.9) * mm, "end": v(-26.1, 240.1) * mm, "construction": true});
            skLineSegment(sketch, "E154.right", {"start": v(-9.9, 233.9) * mm, "end": v(-9.9, 240.1) * mm, "construction": true});
            skPoint(sketch, "E154.middle", {"position": v(-18, 237) * mm});
            skPoint(sketch, "E154.middle.positionSnap0", {"position": v(-83.65, 237) * mm});
            skPoint(sketch, "E154.centerSnap0", {"position": v(-83.65, 237) * mm});
            skArc(sketch, "E155", {"start": v(-23, 240.1) * mm, "mid": v(-26.1, 237) * mm, "end": v(-23, 233.9) * mm});
            skArc(sketch, "E156", {"start": v(-13, 233.9) * mm, "mid": v(-9.9, 237) * mm, "end": v(-13, 240.1) * mm});
            skLineSegment(sketch, "E157.MirrorCS", {"start": v(26.1, 233.9) * mm, "end": v(26.1, 240.1) * mm, "construction": true});
            skLineSegment(sketch, "E158.MirrorCS", {"start": v(9.9, 233.9) * mm, "end": v(9.9, 240.1) * mm, "construction": true});
            skArc(sketch, "E159.MirrorCS", {"start": v(13, 233.9) * mm, "mid": v(9.9, 237) * mm, "end": v(13, 240.1) * mm});
            skArc(sketch, "E160.MirrorCS", {"start": v(23, 240.1) * mm, "mid": v(26.1, 237) * mm, "end": v(23, 233.9) * mm});
            skLineSegment(sketch, "E161.MirrorCS", {"start": v(26.1, 233.9) * mm, "end": v(9.9, 233.9) * mm});
            skLineSegment(sketch, "E162.MirrorCS", {"start": v(26.1, 240.1) * mm, "end": v(9.9, 240.1) * mm});
            skPoint(sketch, "E163.MirrorP", {"position": v(18, 237) * mm});
            skSolve(sketch);
        }
        {
            var Q0;
            {var subQ0=sQuery(id+"F22.wireOp",EDGE,"E155");Q0=makeQuery(id+"F22.imprint","IMPRINT",FACE,{"disambiguationData":[TD([[makeQuery(id+"F22.imprint","IMPRINT",EDGE,{"derivedFrom":subQ0}),1.0]])]});}
            var Q1;
            {var subQ0=sQuery(id+"F22.wireOp",EDGE,"E159.MirrorCS");Q1=makeQuery(id+"F22.imprint","IMPRINT",FACE,{"disambiguationData":[TD([[makeQuery(id+"F22.imprint","IMPRINT",EDGE,{"derivedFrom":subQ0}),-1.0]])]});}
            extrude(context, id + "F23", {"entities" : qUnion([Q0, Q1]), "operationType" : NewBodyOperationType.REMOVE, "oppositeDirection" : true, "depth" : 1 * mm});
        }
        {
            var Q0;
            {var subQ0=sQuery(id+"F0.wireOp",EDGE,"E0.left");var subQ1=sQuery(id+"F0.wireOp",EDGE,"E0.right");Q0=makeQuery(id+"F3.boolean.opBoolean","MERGE",FACE,{"derivedFrom":[makeQuery(id+"F1.opExtrude","CAP_FACE",FACE,{"disambiguationData":[OSD([sQuery(id+"F0.wireOp",EDGE,"E0.bottom"),sQuery(id+"F0.wireOp",EDGE,"E0.top"),subQ0,subQ1])],"isStart":true}),makeQuery(id+"F3.opExtrude","CAP_FACE",FACE,{"disambiguationData":[OSD([subQ1,sQuery(id+"F2.wireOp",EDGE,"E1"),sQuery(id+"F2.wireOp",EDGE,"E2"),sQuery(id+"F2.wireOp",EDGE,"E4.MirrorCS")])],"isStart":false}),makeQuery(id+"F3.opExtrude","CAP_FACE",FACE,{"disambiguationData":[OSD([subQ0,sQuery(id+"F2.wireOp",EDGE,"E6.MirrorCS"),sQuery(id+"F2.wireOp",EDGE,"E8.MirrorCS"),sQuery(id+"F2.wireOp",EDGE,"E9.MirrorCS")])],"isStart":false}),makeQuery(id+"F3.opExtrude","CAP_FACE",FACE,{"disambiguationData":[OSD([subQ1,sQuery(id+"F2.wireOp",EDGE,"E10"),sQuery(id+"F2.wireOp",EDGE,"E11"),sQuery(id+"F2.wireOp",EDGE,"E12")])],"isStart":false}),makeQuery(id+"F3.opExtrude","CAP_FACE",FACE,{"disambiguationData":[OSD([subQ1,sQuery(id+"F2.wireOp",EDGE,"E13"),sQuery(id+"F2.wireOp",EDGE,"E14"),sQuery(id+"F2.wireOp",EDGE,"E15")])],"isStart":false}),makeQuery(id+"F3.opExtrude","CAP_FACE",FACE,{"disambiguationData":[OSD([subQ1,sQuery(id+"F2.wireOp",EDGE,"E16"),sQuery(id+"F2.wireOp",EDGE,"E17"),sQuery(id+"F2.wireOp",EDGE,"E18")])],"isStart":false}),makeQuery(id+"F3.opExtrude","CAP_FACE",FACE,{"disambiguationData":[OSD([subQ1,sQuery(id+"F2.wireOp",EDGE,"E19"),sQuery(id+"F2.wireOp",EDGE,"E20"),sQuery(id+"F2.wireOp",EDGE,"E21")])],"isStart":false}),makeQuery(id+"F3.opExtrude","CAP_FACE",FACE,{"disambiguationData":[OSD([subQ1,sQuery(id+"F2.wireOp",EDGE,"E22"),sQuery(id+"F2.wireOp",EDGE,"E23"),sQuery(id+"F2.wireOp",EDGE,"E24")])],"isStart":false}),makeQuery(id+"F3.opExtrude","CAP_FACE",FACE,{"disambiguationData":[OSD([subQ1,sQuery(id+"F2.wireOp",EDGE,"E25"),sQuery(id+"F2.wireOp",EDGE,"E26"),sQuery(id+"F2.wireOp",EDGE,"E27")])],"isStart":false}),makeQuery(id+"F3.opExtrude","CAP_FACE",FACE,{"disambiguationData":[OSD([subQ1,sQuery(id+"F2.wireOp",EDGE,"E28"),sQuery(id+"F2.wireOp",EDGE,"E29"),sQuery(id+"F2.wireOp",EDGE,"E30")])],"isStart":false}),makeQuery(id+"F3.opExtrude","CAP_FACE",FACE,{"disambiguationData":[OSD([subQ0,sQuery(id+"F2.wireOp",EDGE,"E31.MirrorCS"),sQuery(id+"F2.wireOp",EDGE,"E33.MirrorCS"),sQuery(id+"F2.wireOp",EDGE,"E48.MirrorCS")])],"isStart":false}),makeQuery(id+"F3.opExtrude","CAP_FACE",FACE,{"disambiguationData":[OSD([subQ0,sQuery(id+"F2.wireOp",EDGE,"E32.MirrorCS"),sQuery(id+"F2.wireOp",EDGE,"E46.MirrorCS"),sQuery(id+"F2.wireOp",EDGE,"E49.MirrorCS")])],"isStart":false}),makeQuery(id+"F3.opExtrude","CAP_FACE",FACE,{"disambiguationData":[OSD([subQ0,sQuery(id+"F2.wireOp",EDGE,"E34.MirrorCS"),sQuery(id+"F2.wireOp",EDGE,"E45.MirrorCS"),sQuery(id+"F2.wireOp",EDGE,"E50.MirrorCS")])],"isStart":false}),makeQuery(id+"F3.opExtrude","CAP_FACE",FACE,{"disambiguationData":[OSD([subQ0,sQuery(id+"F2.wireOp",EDGE,"E35.MirrorCS"),sQuery(id+"F2.wireOp",EDGE,"E36.MirrorCS"),sQuery(id+"F2.wireOp",EDGE,"E38.MirrorCS")])],"isStart":false}),makeQuery(id+"F3.opExtrude","CAP_FACE",FACE,{"disambiguationData":[OSD([subQ0,sQuery(id+"F2.wireOp",EDGE,"E37.MirrorCS"),sQuery(id+"F2.wireOp",EDGE,"E39.MirrorCS"),sQuery(id+"F2.wireOp",EDGE,"E43.MirrorCS")])],"isStart":false}),makeQuery(id+"F3.opExtrude","CAP_FACE",FACE,{"disambiguationData":[OSD([subQ0,sQuery(id+"F2.wireOp",EDGE,"E40.MirrorCS"),sQuery(id+"F2.wireOp",EDGE,"E44.MirrorCS"),sQuery(id+"F2.wireOp",EDGE,"E51.MirrorCS")])],"isStart":false}),makeQuery(id+"F3.opExtrude","CAP_FACE",FACE,{"disambiguationData":[OSD([subQ0,sQuery(id+"F2.wireOp",EDGE,"E41.MirrorCS"),sQuery(id+"F2.wireOp",EDGE,"E42.MirrorCS"),sQuery(id+"F2.wireOp",EDGE,"E47.MirrorCS")])],"isStart":false})]});}
            var sketch = newSketch(context, id + "F24", { "sketchPlane" : qUnion([Q0])});
            skLineSegment(sketch, "E164.bottom", {"start": v(-11.5, 240.1) * mm, "end": v(-24.5, 240.1) * mm});
            skLineSegment(sketch, "E164.top", {"start": v(-11.5, 237.1) * mm, "end": v(-13, 237.1) * mm, "construction": true});
            skLineSegment(sketch, "E164.left", {"start": v(-11.5, 240.1) * mm, "end": v(-11.5, 237.1) * mm, "construction": true});
            skLineSegment(sketch, "E164.right", {"start": v(-24.5, 240.1) * mm, "end": v(-24.5, 237.1) * mm, "construction": true});
            skPoint(sketch, "E164.middle", {"position": v(-18, 238.6) * mm});
            skPoint(sketch, "E164.middle.positionSnap0", {"position": v(-18, 240.1) * mm});
            skPoint(sketch, "E164.cornerSnap0", {"position": v(-18, 240.1) * mm});
            skPoint(sketch, "E164.centerSnap0", {"position": v(-18, 240.1) * mm});
            skLineSegment(sketch, "E165.top", {"start": v(-13, 232.4) * mm, "end": v(-23, 232.4) * mm});
            skLineSegment(sketch, "E165.left", {"start": v(-13, 237.1) * mm, "end": v(-13, 232.4) * mm});
            skLineSegment(sketch, "E165.right", {"start": v(-23, 237.1) * mm, "end": v(-23, 232.4) * mm});
            skPoint(sketch, "E165.middle", {"position": v(-18, 234.75) * mm});
            skLineSegment(sketch, "E166.trimOffspring", {"start": v(-23, 237.1) * mm, "end": v(-24.5, 237.1) * mm, "construction": true});
            skArc(sketch, "E167", {"start": v(-23, 240.1) * mm, "mid": v(-24.5, 238.6) * mm, "end": v(-23, 237.1) * mm});
            skLineSegment(sketch, "E168", {"start": v(-18, 234.75) * mm, "end": v(-18, 240.1) * mm, "construction": true});
            skArc(sketch, "E169", {"start": v(-23, 233.9) * mm, "mid": v(-22.56, 232.84) * mm, "end": v(-21.5, 232.4) * mm});
            skArc(sketch, "E170.MirrorCS", {"start": v(-13, 240.1) * mm, "mid": v(-11.5, 238.6) * mm, "end": v(-13, 237.1) * mm});
            skArc(sketch, "E171.MirrorCS", {"start": v(-13, 233.9) * mm, "mid": v(-13.44, 232.84) * mm, "end": v(-14.5, 232.4) * mm});
            skLineSegment(sketch, "E172.MirrorCS", {"start": v(11.5, 237.1) * mm, "end": v(13, 237.1) * mm, "construction": true});
            skLineSegment(sketch, "E173.MirrorCS", {"start": v(11.5, 240.1) * mm, "end": v(11.5, 237.1) * mm, "construction": true});
            skArc(sketch, "E174.MirrorCS", {"start": v(13, 240.1) * mm, "mid": v(11.5, 238.6) * mm, "end": v(13, 237.1) * mm});
            skLineSegment(sketch, "E175.MirrorCS", {"start": v(24.5, 240.1) * mm, "end": v(24.5, 237.1) * mm, "construction": true});
            skArc(sketch, "E176.MirrorCS", {"start": v(23, 240.1) * mm, "mid": v(24.5, 238.6) * mm, "end": v(23, 237.1) * mm});
            skLineSegment(sketch, "E177.MirrorCS", {"start": v(23, 237.1) * mm, "end": v(24.5, 237.1) * mm, "construction": true});
            skArc(sketch, "E178.MirrorCS", {"start": v(13, 233.9) * mm, "mid": v(13.44, 232.84) * mm, "end": v(14.5, 232.4) * mm});
            skLineSegment(sketch, "E179.MirrorCS", {"start": v(13, 237.1) * mm, "end": v(13, 232.4) * mm});
            skLineSegment(sketch, "E180.MirrorCS", {"start": v(11.5, 240.1) * mm, "end": v(24.5, 240.1) * mm});
            skPoint(sketch, "E181.MirrorP", {"position": v(18, 240.1) * mm});
            skLineSegment(sketch, "E182.MirrorCS", {"start": v(18, 234.75) * mm, "end": v(18, 240.1) * mm, "construction": true});
            skArc(sketch, "E183.MirrorCS", {"start": v(23, 233.9) * mm, "mid": v(22.56, 232.84) * mm, "end": v(21.5, 232.4) * mm});
            skLineSegment(sketch, "E184.MirrorCS", {"start": v(23, 237.1) * mm, "end": v(23, 232.4) * mm});
            skPoint(sketch, "E185.MirrorP", {"position": v(18, 238.6) * mm});
            skLineSegment(sketch, "E186.MirrorCS", {"start": v(13, 232.4) * mm, "end": v(23, 232.4) * mm});
            skPoint(sketch, "E187.MirrorP", {"position": v(18, 234.75) * mm});
            skSolve(sketch);
        }
        {
            var Q0;
            {var subQ0=sQuery(id+"F24.wireOp",EDGE,"E167");Q0=makeQuery(id+"F24.imprint","IMPRINT",FACE,{"disambiguationData":[TD([[makeQuery(id+"F24.imprint","IMPRINT",EDGE,{"derivedFrom":subQ0}),1.0]])]});}
            var Q1;
            {var subQ0=sQuery(id+"F24.wireOp",EDGE,"E169");Q1=makeQuery(id+"F24.imprint","IMPRINT",FACE,{"disambiguationData":[TD([[makeQuery(id+"F24.imprint","IMPRINT",EDGE,{"derivedFrom":subQ0}),1.0]])]});}
            var Q2;
            {var subQ3=sQuery(id+"F24.wireOp",EDGE,"E174.MirrorCS");Q2=makeQuery(id+"F24.imprint","IMPRINT",FACE,{"disambiguationData":[TD([[makeQuery(id+"F24.imprint","IMPRINT",EDGE,{"derivedFrom":subQ3}),1.0]])]});}
            var Q3;
            {var subQ0=sQuery(id+"F24.wireOp",EDGE,"E178.MirrorCS");Q3=makeQuery(id+"F24.imprint","IMPRINT",FACE,{"disambiguationData":[TD([[makeQuery(id+"F24.imprint","IMPRINT",EDGE,{"derivedFrom":subQ0}),1.0]])]});}
            extrude(context, id + "F25", {"entities" : qUnion([Q0, Q1, Q2, Q3]), "operationType" : NewBodyOperationType.REMOVE, "oppositeDirection" : true, "depth" : 4.5 * mm});
        }
    });
